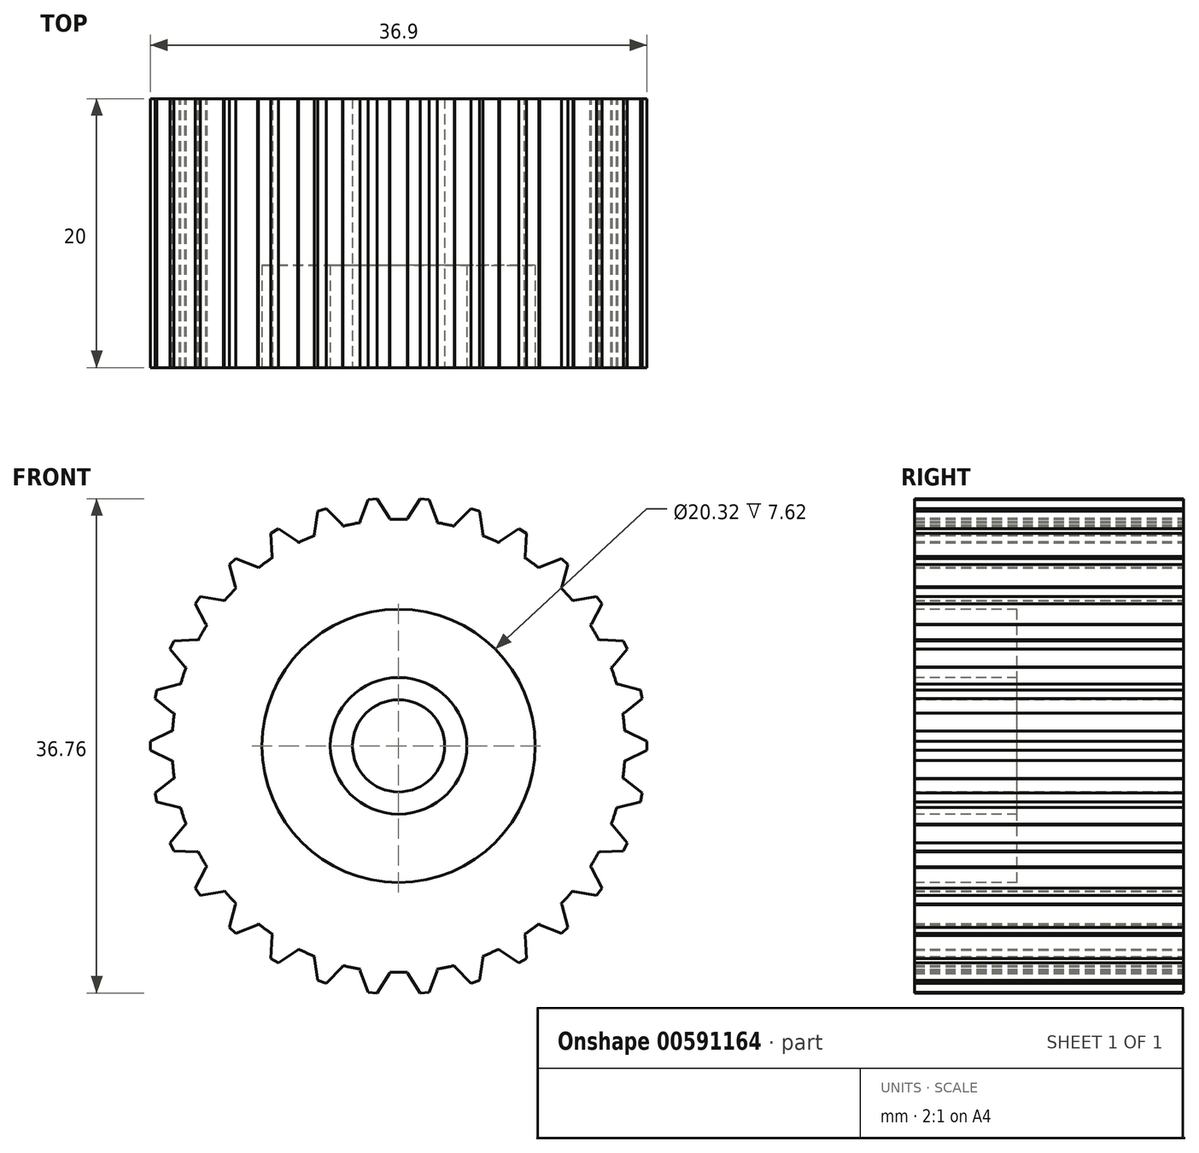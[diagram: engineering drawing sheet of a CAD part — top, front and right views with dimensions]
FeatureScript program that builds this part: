
annotation { "Feature Type Name" : "Feature", "Feature Type Description" : "" }
export const myFeature = defineFeature(function(context is Context, id is Id, definition is map)
    precondition{}
    {
        {
            var Q0;
            Q0=qCreatedBy(makeId("Front.planeOp"),FACE);
            var sketch = newSketch(context, id + "F0", { "sketchPlane" : qUnion([Q0])});
            skCircle(sketch, "E0", {"center": v(0, 0) * mm, "radius": 16.85 * mm});
            skLineSegment(sketch, "E1", {"start": v(0, 0) * mm, "end": v(16.85, 0) * mm, "construction": true});
            skLineSegment(sketch, "E2", {"start": v(16.85, 0) * mm, "end": v(18.45, 0) * mm, "construction": true});
            skLineSegment(sketch, "E3", {"start": v(18.45, 0) * mm, "end": v(18.45, 0.33) * mm});
            skLineSegment(sketch, "E4", {"start": v(16.81, 1.1) * mm, "end": v(16.91, 1.1) * mm});
            skLineSegment(sketch, "E5", {"start": v(16.91, 1.1) * mm, "end": v(18.45, 0.33) * mm});
            skLineSegment(sketch, "E6.MirrorCS", {"start": v(16.91, -1.1) * mm, "end": v(18.45, -0.33) * mm});
            skLineSegment(sketch, "E7.MirrorCS", {"start": v(18.45, 0) * mm, "end": v(18.45, -0.33) * mm});
            skLineSegment(sketch, "E8.MirrorCS", {"start": v(16.81, -1.1) * mm, "end": v(16.91, -1.1) * mm});
            skLineSegment(sketch, "E9.2.0", {"start": v(-72.23, -20.11) * mm, "end": v(-72.15, -20.06) * mm});
            skLineSegment(sketch, "E9.2.1", {"start": v(-72.15, -20.06) * mm, "end": v(-71.63, -19.91) * mm});
            skLineSegment(sketch, "E9.2.2", {"start": v(-71.45, -20.19) * mm, "end": v(-71.63, -19.91) * mm});
            skLineSegment(sketch, "E9.2.3", {"start": v(-71.45, -20.19) * mm, "end": v(-71.26, -20.46) * mm});
            skLineSegment(sketch, "E9.2.4", {"start": v(-71.58, -20.88) * mm, "end": v(-71.26, -20.46) * mm});
            skLineSegment(sketch, "E9.2.5", {"start": v(-71.67, -20.94) * mm, "end": v(-71.58, -20.88) * mm});
            skLineSegment(sketch, "E9.3.0", {"start": v(-108.67, -49.23) * mm, "end": v(-108.6, -49.15) * mm});
            skLineSegment(sketch, "E9.3.1", {"start": v(-108.6, -49.15) * mm, "end": v(-108.16, -48.86) * mm});
            skLineSegment(sketch, "E9.3.2", {"start": v(-107.9, -49.07) * mm, "end": v(-108.16, -48.86) * mm});
            skLineSegment(sketch, "E9.3.3", {"start": v(-107.9, -49.07) * mm, "end": v(-107.64, -49.28) * mm});
            skLineSegment(sketch, "E9.3.4", {"start": v(-107.83, -49.78) * mm, "end": v(-107.64, -49.28) * mm});
            skLineSegment(sketch, "E9.3.5", {"start": v(-107.89, -49.86) * mm, "end": v(-107.83, -49.78) * mm});
            skLineSegment(sketch, "E9.4.0", {"start": v(-134.91, -87.8) * mm, "end": v(-134.88, -87.7) * mm});
            skLineSegment(sketch, "E9.4.1", {"start": v(-134.88, -87.7) * mm, "end": v(-134.53, -87.3) * mm});
            skLineSegment(sketch, "E9.4.2", {"start": v(-134.23, -87.42) * mm, "end": v(-134.53, -87.3) * mm});
            skLineSegment(sketch, "E9.4.3", {"start": v(-134.23, -87.42) * mm, "end": v(-133.92, -87.54) * mm});
            skLineSegment(sketch, "E9.4.4", {"start": v(-133.95, -88.07) * mm, "end": v(-133.92, -87.54) * mm});
            skLineSegment(sketch, "E9.4.5", {"start": v(-133.98, -88.17) * mm, "end": v(-133.95, -88.07) * mm});
            skLineSegment(sketch, "E9.5.0", {"start": v(-148.62, -132.39) * mm, "end": v(-148.61, -132.29) * mm});
            skLineSegment(sketch, "E9.5.1", {"start": v(-148.61, -132.29) * mm, "end": v(-148.4, -131.8) * mm});
            skLineSegment(sketch, "E9.5.2", {"start": v(-148.08, -131.82) * mm, "end": v(-148.4, -131.8) * mm});
            skLineSegment(sketch, "E9.5.3", {"start": v(-148.08, -131.82) * mm, "end": v(-147.75, -131.85) * mm});
            skLineSegment(sketch, "E9.5.4", {"start": v(-147.62, -132.36) * mm, "end": v(-147.75, -131.85) * mm});
            skLineSegment(sketch, "E9.5.5", {"start": v(-147.62, -132.46) * mm, "end": v(-147.62, -132.36) * mm});
            skLineSegment(sketch, "E9.6.0", {"start": v(-148.58, -179.04) * mm, "end": v(-148.6, -178.94) * mm});
            skLineSegment(sketch, "E9.6.1", {"start": v(-148.6, -178.94) * mm, "end": v(-148.54, -178.4) * mm});
            skLineSegment(sketch, "E9.6.2", {"start": v(-148.22, -178.33) * mm, "end": v(-148.54, -178.4) * mm});
            skLineSegment(sketch, "E9.6.3", {"start": v(-148.22, -178.33) * mm, "end": v(-147.9, -178.26) * mm});
            skLineSegment(sketch, "E9.6.4", {"start": v(-147.62, -178.72) * mm, "end": v(-147.9, -178.26) * mm});
            skLineSegment(sketch, "E9.6.5", {"start": v(-147.6, -178.81) * mm, "end": v(-147.62, -178.72) * mm});
            skLineSegment(sketch, "E9.7.0", {"start": v(-134.78, -223.6) * mm, "end": v(-134.83, -223.51) * mm});
            skLineSegment(sketch, "E9.7.1", {"start": v(-134.83, -223.51) * mm, "end": v(-134.94, -222.99) * mm});
            skLineSegment(sketch, "E9.7.2", {"start": v(-134.65, -222.82) * mm, "end": v(-134.94, -222.99) * mm});
            skLineSegment(sketch, "E9.7.3", {"start": v(-134.65, -222.82) * mm, "end": v(-134.37, -222.66) * mm});
            skLineSegment(sketch, "E9.7.4", {"start": v(-133.97, -223.01) * mm, "end": v(-134.37, -222.66) * mm});
            skLineSegment(sketch, "E9.7.5", {"start": v(-133.92, -223.1) * mm, "end": v(-133.97, -223.01) * mm});
            skLineSegment(sketch, "E9.8.0", {"start": v(-108.47, -262.12) * mm, "end": v(-108.54, -262.05) * mm});
            skLineSegment(sketch, "E9.8.1", {"start": v(-108.54, -262.05) * mm, "end": v(-108.8, -261.58) * mm});
            skLineSegment(sketch, "E9.8.2", {"start": v(-108.57, -261.34) * mm, "end": v(-108.8, -261.58) * mm});
            skLineSegment(sketch, "E9.8.3", {"start": v(-108.57, -261.34) * mm, "end": v(-108.35, -261.1) * mm});
            skLineSegment(sketch, "E9.8.4", {"start": v(-107.86, -261.32) * mm, "end": v(-108.35, -261.1) * mm});
            skLineSegment(sketch, "E9.8.5", {"start": v(-107.79, -261.38) * mm, "end": v(-107.86, -261.32) * mm});
            skLineSegment(sketch, "E9.9.0", {"start": v(-71.97, -291.17) * mm, "end": v(-72.06, -291.12) * mm});
            skLineSegment(sketch, "E9.9.1", {"start": v(-72.06, -291.12) * mm, "end": v(-72.44, -290.75) * mm});
            skLineSegment(sketch, "E9.9.2", {"start": v(-72.3, -290.45) * mm, "end": v(-72.44, -290.75) * mm});
            skLineSegment(sketch, "E9.9.3", {"start": v(-72.3, -290.45) * mm, "end": v(-72.16, -290.16) * mm});
            skLineSegment(sketch, "E9.9.4", {"start": v(-71.63, -290.22) * mm, "end": v(-72.16, -290.16) * mm});
            skLineSegment(sketch, "E9.9.5", {"start": v(-71.54, -290.27) * mm, "end": v(-71.63, -290.22) * mm});
            skLineSegment(sketch, "E9.10.0", {"start": v(-28.53, -308.17) * mm, "end": v(-28.63, -308.15) * mm});
            skLineSegment(sketch, "E9.10.1", {"start": v(-28.63, -308.15) * mm, "end": v(-29.1, -307.9) * mm});
            skLineSegment(sketch, "E9.10.2", {"start": v(-29.06, -307.58) * mm, "end": v(-29.1, -307.9) * mm});
            skLineSegment(sketch, "E9.10.3", {"start": v(-29.06, -307.58) * mm, "end": v(-29, -307.26) * mm});
            skLineSegment(sketch, "E9.10.4", {"start": v(-28.48, -307.16) * mm, "end": v(-29, -307.26) * mm});
            skLineSegment(sketch, "E9.10.5", {"start": v(-28.38, -307.18) * mm, "end": v(-28.48, -307.16) * mm});
            skLineSegment(sketch, "E9.11.0", {"start": v(17.99, -311.6) * mm, "end": v(17.9, -311.62) * mm});
            skLineSegment(sketch, "E9.11.1", {"start": v(17.9, -311.62) * mm, "end": v(17.36, -311.53) * mm});
            skLineSegment(sketch, "E9.11.2", {"start": v(17.31, -311.2) * mm, "end": v(17.36, -311.53) * mm});
            skLineSegment(sketch, "E9.11.3", {"start": v(17.31, -311.2) * mm, "end": v(17.27, -310.88) * mm});
            skLineSegment(sketch, "E9.11.4", {"start": v(17.74, -310.64) * mm, "end": v(17.27, -310.88) * mm});
            skLineSegment(sketch, "E9.11.5", {"start": v(17.84, -310.62) * mm, "end": v(17.74, -310.64) * mm});
            skLineSegment(sketch, "E9.12.0", {"start": v(63.46, -301.19) * mm, "end": v(63.37, -301.23) * mm});
            skLineSegment(sketch, "E9.12.1", {"start": v(63.37, -301.23) * mm, "end": v(62.84, -301.3) * mm});
            skLineSegment(sketch, "E9.12.2", {"start": v(62.7, -301) * mm, "end": v(62.84, -301.3) * mm});
            skLineSegment(sketch, "E9.12.3", {"start": v(62.7, -301) * mm, "end": v(62.55, -300.7) * mm});
            skLineSegment(sketch, "E9.12.4", {"start": v(62.93, -300.33) * mm, "end": v(62.55, -300.7) * mm});
            skLineSegment(sketch, "E9.12.5", {"start": v(63.02, -300.28) * mm, "end": v(62.93, -300.33) * mm});
            skLineSegment(sketch, "E9.13.0", {"start": v(103.83, -277.82) * mm, "end": v(103.76, -277.9) * mm});
            skLineSegment(sketch, "E9.13.1", {"start": v(103.76, -277.9) * mm, "end": v(103.27, -278.11) * mm});
            skLineSegment(sketch, "E9.13.2", {"start": v(103.05, -277.87) * mm, "end": v(103.27, -278.11) * mm});
            skLineSegment(sketch, "E9.13.3", {"start": v(103.05, -277.87) * mm, "end": v(102.82, -277.63) * mm});
            skLineSegment(sketch, "E9.13.4", {"start": v(103.08, -277.16) * mm, "end": v(102.82, -277.63) * mm});
            skLineSegment(sketch, "E9.13.5", {"start": v(103.15, -277.1) * mm, "end": v(103.08, -277.16) * mm});
            skLineSegment(sketch, "E9.14.0", {"start": v(135.53, -243.6) * mm, "end": v(135.48, -243.68) * mm});
            skLineSegment(sketch, "E9.14.1", {"start": v(135.48, -243.68) * mm, "end": v(135.08, -244.04) * mm});
            skLineSegment(sketch, "E9.14.2", {"start": v(134.8, -243.87) * mm, "end": v(135.08, -244.04) * mm});
            skLineSegment(sketch, "E9.14.3", {"start": v(134.8, -243.87) * mm, "end": v(134.5, -243.7) * mm});
            skLineSegment(sketch, "E9.14.4", {"start": v(134.61, -243.18) * mm, "end": v(134.5, -243.7) * mm});
            skLineSegment(sketch, "E9.14.5", {"start": v(134.66, -243.1) * mm, "end": v(134.61, -243.18) * mm});
            skLineSegment(sketch, "E9.15.0", {"start": v(155.73, -201.55) * mm, "end": v(155.7, -201.65) * mm});
            skLineSegment(sketch, "E9.15.1", {"start": v(155.7, -201.65) * mm, "end": v(155.43, -202.1) * mm});
            skLineSegment(sketch, "E9.15.2", {"start": v(155.1, -202.03) * mm, "end": v(155.43, -202.1) * mm});
            skLineSegment(sketch, "E9.15.3", {"start": v(155.1, -202.03) * mm, "end": v(154.79, -201.96) * mm});
            skLineSegment(sketch, "E9.15.4", {"start": v(154.73, -201.43) * mm, "end": v(154.79, -201.96) * mm});
            skLineSegment(sketch, "E9.15.5", {"start": v(154.76, -201.33) * mm, "end": v(154.73, -201.43) * mm});
            skLineSegment(sketch, "E9.16.0", {"start": v(162.64, -155.42) * mm, "end": v(162.65, -155.52) * mm});
            skLineSegment(sketch, "E9.16.1", {"start": v(162.65, -155.52) * mm, "end": v(162.51, -156.04) * mm});
            skLineSegment(sketch, "E9.16.2", {"start": v(162.19, -156.06) * mm, "end": v(162.51, -156.04) * mm});
            skLineSegment(sketch, "E9.16.3", {"start": v(162.19, -156.06) * mm, "end": v(161.86, -156.08) * mm});
            skLineSegment(sketch, "E9.16.4", {"start": v(161.65, -155.6) * mm, "end": v(161.86, -156.08) * mm});
            skLineSegment(sketch, "E9.16.5", {"start": v(161.64, -155.5) * mm, "end": v(161.65, -155.6) * mm});
            skLineSegment(sketch, "E9.17.0", {"start": v(155.64, -109.3) * mm, "end": v(155.68, -109.39) * mm});
            skLineSegment(sketch, "E9.17.1", {"start": v(155.68, -109.39) * mm, "end": v(155.7, -109.92) * mm});
            skLineSegment(sketch, "E9.17.2", {"start": v(155.4, -110.04) * mm, "end": v(155.7, -109.92) * mm});
            skLineSegment(sketch, "E9.17.3", {"start": v(155.4, -110.04) * mm, "end": v(155.1, -110.17) * mm});
            skLineSegment(sketch, "E9.17.4", {"start": v(154.75, -109.76) * mm, "end": v(155.1, -110.17) * mm});
            skLineSegment(sketch, "E9.17.5", {"start": v(154.71, -109.66) * mm, "end": v(154.75, -109.76) * mm});
            skLineSegment(sketch, "E9.18.0", {"start": v(135.36, -67.29) * mm, "end": v(135.43, -67.37) * mm});
            skLineSegment(sketch, "E9.18.1", {"start": v(135.43, -67.37) * mm, "end": v(135.6, -67.87) * mm});
            skLineSegment(sketch, "E9.18.2", {"start": v(135.35, -68.07) * mm, "end": v(135.6, -67.87) * mm});
            skLineSegment(sketch, "E9.18.3", {"start": v(135.35, -68.07) * mm, "end": v(135.1, -68.28) * mm});
            skLineSegment(sketch, "E9.18.4", {"start": v(134.64, -67.99) * mm, "end": v(135.1, -68.28) * mm});
            skLineSegment(sketch, "E9.18.5", {"start": v(134.58, -67.91) * mm, "end": v(134.64, -67.99) * mm});
            skLineSegment(sketch, "E9.19.0", {"start": v(103.6, -33.12) * mm, "end": v(103.68, -33.18) * mm});
            skLineSegment(sketch, "E9.19.1", {"start": v(103.68, -33.18) * mm, "end": v(104, -33.6) * mm});
            skLineSegment(sketch, "E9.19.2", {"start": v(103.82, -33.88) * mm, "end": v(104, -33.6) * mm});
            skLineSegment(sketch, "E9.19.3", {"start": v(103.82, -33.88) * mm, "end": v(103.64, -34.15) * mm});
            skLineSegment(sketch, "E9.19.4", {"start": v(103.12, -34) * mm, "end": v(103.64, -34.15) * mm});
            skLineSegment(sketch, "E9.19.5", {"start": v(103.04, -33.95) * mm, "end": v(103.12, -34) * mm});
            skLineSegment(sketch, "E9.20.0", {"start": v(63.18, -9.84) * mm, "end": v(63.28, -9.87) * mm});
            skLineSegment(sketch, "E9.20.1", {"start": v(63.28, -9.87) * mm, "end": v(63.71, -10.18) * mm});
            skLineSegment(sketch, "E9.20.2", {"start": v(63.61, -10.5) * mm, "end": v(63.71, -10.18) * mm});
            skLineSegment(sketch, "E9.20.3", {"start": v(63.61, -10.5) * mm, "end": v(63.52, -10.8) * mm});
            skLineSegment(sketch, "E9.20.4", {"start": v(62.98, -10.82) * mm, "end": v(63.52, -10.8) * mm});
            skLineSegment(sketch, "E9.20.5", {"start": v(62.89, -10.8) * mm, "end": v(62.98, -10.82) * mm});
            skPoint(sketch, "E10.center", {"position": v(-0.17, 0) * mm});
            skLineSegment(sketch, "E11.1.0", {"start": v(16.22, 4.57) * mm, "end": v(16.32, 4.6) * mm});
            skLineSegment(sketch, "E11.1.1", {"start": v(16.32, 4.6) * mm, "end": v(17.98, 4.16) * mm});
            skLineSegment(sketch, "E11.1.2", {"start": v(18.05, 3.84) * mm, "end": v(17.98, 4.16) * mm});
            skLineSegment(sketch, "E11.1.3", {"start": v(18.05, 3.84) * mm, "end": v(18.12, 3.51) * mm});
            skLineSegment(sketch, "E11.1.4", {"start": v(16.77, 2.44) * mm, "end": v(18.12, 3.51) * mm});
            skLineSegment(sketch, "E11.1.5", {"start": v(16.68, 2.42) * mm, "end": v(16.77, 2.44) * mm});
            skLineSegment(sketch, "E11.2.0", {"start": v(14.91, 7.84) * mm, "end": v(15, 7.88) * mm});
            skLineSegment(sketch, "E11.2.1", {"start": v(15, 7.88) * mm, "end": v(16.72, 7.8) * mm});
            skLineSegment(sketch, "E11.2.2", {"start": v(16.85, 7.5) * mm, "end": v(16.72, 7.8) * mm});
            skLineSegment(sketch, "E11.2.3", {"start": v(16.85, 7.5) * mm, "end": v(16.99, 7.2) * mm});
            skLineSegment(sketch, "E11.2.4", {"start": v(15.9, 5.87) * mm, "end": v(16.99, 7.2) * mm});
            skLineSegment(sketch, "E11.2.5", {"start": v(15.8, 5.83) * mm, "end": v(15.9, 5.87) * mm});
            skLineSegment(sketch, "E11.3.0", {"start": v(12.96, 10.77) * mm, "end": v(13.04, 10.83) * mm});
            skLineSegment(sketch, "E11.3.1", {"start": v(13.04, 10.83) * mm, "end": v(14.73, 11.11) * mm});
            skLineSegment(sketch, "E11.3.2", {"start": v(14.93, 10.84) * mm, "end": v(14.73, 11.11) * mm});
            skLineSegment(sketch, "E11.3.3", {"start": v(14.93, 10.84) * mm, "end": v(15.12, 10.58) * mm});
            skLineSegment(sketch, "E11.3.4", {"start": v(14.33, 9.05) * mm, "end": v(15.12, 10.58) * mm});
            skLineSegment(sketch, "E11.3.5", {"start": v(14.25, 9) * mm, "end": v(14.33, 9.05) * mm});
            skLineSegment(sketch, "E11.4.0", {"start": v(10.43, 13.23) * mm, "end": v(10.5, 13.3) * mm});
            skLineSegment(sketch, "E11.4.1", {"start": v(10.5, 13.3) * mm, "end": v(12.1, 13.93) * mm});
            skLineSegment(sketch, "E11.4.2", {"start": v(12.35, 13.71) * mm, "end": v(12.1, 13.93) * mm});
            skLineSegment(sketch, "E11.4.3", {"start": v(12.35, 13.71) * mm, "end": v(12.6, 13.5) * mm});
            skLineSegment(sketch, "E11.4.4", {"start": v(12.14, 11.83) * mm, "end": v(12.6, 13.5) * mm});
            skLineSegment(sketch, "E11.4.5", {"start": v(12.07, 11.76) * mm, "end": v(12.14, 11.83) * mm});
            skLineSegment(sketch, "E11.5.0", {"start": v(7.45, 15.11) * mm, "end": v(7.5, 15.2) * mm});
            skLineSegment(sketch, "E11.5.1", {"start": v(7.5, 15.2) * mm, "end": v(8.94, 16.14) * mm});
            skLineSegment(sketch, "E11.5.2", {"start": v(9.22, 15.98) * mm, "end": v(8.94, 16.14) * mm});
            skLineSegment(sketch, "E11.5.3", {"start": v(9.23, 15.98) * mm, "end": v(9.51, 15.81) * mm});
            skLineSegment(sketch, "E11.5.4", {"start": v(9.4, 14.1) * mm, "end": v(9.51, 15.81) * mm});
            skLineSegment(sketch, "E11.5.5", {"start": v(9.36, 14.01) * mm, "end": v(9.4, 14.1) * mm});
            skLineSegment(sketch, "E11.6.0", {"start": v(4.15, 16.33) * mm, "end": v(4.18, 16.43) * mm});
            skLineSegment(sketch, "E11.6.1", {"start": v(4.18, 16.43) * mm, "end": v(5.39, 17.65) * mm});
            skLineSegment(sketch, "E11.6.2", {"start": v(5.7, 17.55) * mm, "end": v(5.39, 17.65) * mm});
            skLineSegment(sketch, "E11.6.3", {"start": v(5.7, 17.55) * mm, "end": v(6.02, 17.45) * mm});
            skLineSegment(sketch, "E11.6.4", {"start": v(6.27, 15.75) * mm, "end": v(6.02, 17.45) * mm});
            skLineSegment(sketch, "E11.6.5", {"start": v(6.24, 15.65) * mm, "end": v(6.27, 15.75) * mm});
            skLineSegment(sketch, "E11.7.0", {"start": v(0.66, 16.84) * mm, "end": v(0.67, 16.94) * mm});
            skLineSegment(sketch, "E11.7.1", {"start": v(0.67, 16.94) * mm, "end": v(1.6, 18.38) * mm});
            skLineSegment(sketch, "E11.7.2", {"start": v(1.93, 18.35) * mm, "end": v(1.6, 18.38) * mm});
            skLineSegment(sketch, "E11.7.3", {"start": v(1.93, 18.35) * mm, "end": v(2.26, 18.31) * mm});
            skLineSegment(sketch, "E11.7.4", {"start": v(2.86, 16.7) * mm, "end": v(2.26, 18.31) * mm});
            skLineSegment(sketch, "E11.7.5", {"start": v(2.85, 16.6) * mm, "end": v(2.86, 16.7) * mm});
            skLineSegment(sketch, "E11.8.0", {"start": v(-2.85, 16.6) * mm, "end": v(-2.86, 16.7) * mm});
            skLineSegment(sketch, "E11.8.1", {"start": v(-2.86, 16.7) * mm, "end": v(-2.26, 18.31) * mm});
            skLineSegment(sketch, "E11.8.2", {"start": v(-1.93, 18.35) * mm, "end": v(-2.26, 18.31) * mm});
            skLineSegment(sketch, "E11.8.3", {"start": v(-1.93, 18.35) * mm, "end": v(-1.6, 18.38) * mm});
            skLineSegment(sketch, "E11.8.4", {"start": v(-0.67, 16.94) * mm, "end": v(-1.6, 18.38) * mm});
            skLineSegment(sketch, "E11.8.5", {"start": v(-0.66, 16.84) * mm, "end": v(-0.67, 16.94) * mm});
            skLineSegment(sketch, "E11.9.0", {"start": v(-6.24, 15.65) * mm, "end": v(-6.27, 15.75) * mm});
            skLineSegment(sketch, "E11.9.1", {"start": v(-6.27, 15.75) * mm, "end": v(-6.02, 17.45) * mm});
            skLineSegment(sketch, "E11.9.2", {"start": v(-5.7, 17.55) * mm, "end": v(-6.02, 17.45) * mm});
            skLineSegment(sketch, "E11.9.3", {"start": v(-5.7, 17.55) * mm, "end": v(-5.39, 17.65) * mm});
            skLineSegment(sketch, "E11.9.4", {"start": v(-4.18, 16.43) * mm, "end": v(-5.39, 17.65) * mm});
            skLineSegment(sketch, "E11.9.5", {"start": v(-4.15, 16.33) * mm, "end": v(-4.18, 16.43) * mm});
            skLineSegment(sketch, "E11.10.0", {"start": v(-9.36, 14.01) * mm, "end": v(-9.4, 14.1) * mm});
            skLineSegment(sketch, "E11.10.1", {"start": v(-9.4, 14.1) * mm, "end": v(-9.51, 15.81) * mm});
            skLineSegment(sketch, "E11.10.2", {"start": v(-9.23, 15.98) * mm, "end": v(-9.51, 15.81) * mm});
            skLineSegment(sketch, "E11.10.3", {"start": v(-9.23, 15.98) * mm, "end": v(-8.94, 16.14) * mm});
            skLineSegment(sketch, "E11.10.4", {"start": v(-7.5, 15.2) * mm, "end": v(-8.94, 16.14) * mm});
            skLineSegment(sketch, "E11.10.5", {"start": v(-7.45, 15.11) * mm, "end": v(-7.5, 15.2) * mm});
            skLineSegment(sketch, "E11.11.0", {"start": v(-12.07, 11.76) * mm, "end": v(-12.14, 11.83) * mm});
            skLineSegment(sketch, "E11.11.1", {"start": v(-12.14, 11.83) * mm, "end": v(-12.6, 13.5) * mm});
            skLineSegment(sketch, "E11.11.2", {"start": v(-12.35, 13.71) * mm, "end": v(-12.6, 13.5) * mm});
            skLineSegment(sketch, "E11.11.3", {"start": v(-12.35, 13.71) * mm, "end": v(-12.1, 13.93) * mm});
            skLineSegment(sketch, "E11.11.4", {"start": v(-10.5, 13.3) * mm, "end": v(-12.1, 13.93) * mm});
            skLineSegment(sketch, "E11.11.5", {"start": v(-10.43, 13.23) * mm, "end": v(-10.5, 13.3) * mm});
            skLineSegment(sketch, "E11.12.0", {"start": v(-14.25, 9) * mm, "end": v(-14.33, 9.05) * mm});
            skLineSegment(sketch, "E11.12.1", {"start": v(-14.33, 9.05) * mm, "end": v(-15.12, 10.58) * mm});
            skLineSegment(sketch, "E11.12.2", {"start": v(-14.93, 10.84) * mm, "end": v(-15.12, 10.58) * mm});
            skLineSegment(sketch, "E11.12.3", {"start": v(-14.93, 10.84) * mm, "end": v(-14.73, 11.11) * mm});
            skLineSegment(sketch, "E11.12.4", {"start": v(-13.04, 10.83) * mm, "end": v(-14.73, 11.11) * mm});
            skLineSegment(sketch, "E11.12.5", {"start": v(-12.96, 10.77) * mm, "end": v(-13.04, 10.83) * mm});
            skLineSegment(sketch, "E11.13.0", {"start": v(-15.8, 5.83) * mm, "end": v(-15.9, 5.87) * mm});
            skLineSegment(sketch, "E11.13.1", {"start": v(-15.9, 5.87) * mm, "end": v(-16.99, 7.2) * mm});
            skLineSegment(sketch, "E11.13.2", {"start": v(-16.85, 7.5) * mm, "end": v(-16.99, 7.2) * mm});
            skLineSegment(sketch, "E11.13.3", {"start": v(-16.85, 7.5) * mm, "end": v(-16.72, 7.8) * mm});
            skLineSegment(sketch, "E11.13.4", {"start": v(-15, 7.88) * mm, "end": v(-16.72, 7.8) * mm});
            skLineSegment(sketch, "E11.13.5", {"start": v(-14.91, 7.84) * mm, "end": v(-15, 7.88) * mm});
            skLineSegment(sketch, "E11.14.0", {"start": v(-16.68, 2.42) * mm, "end": v(-16.77, 2.44) * mm});
            skLineSegment(sketch, "E11.14.1", {"start": v(-16.77, 2.44) * mm, "end": v(-18.12, 3.51) * mm});
            skLineSegment(sketch, "E11.14.2", {"start": v(-18.05, 3.84) * mm, "end": v(-18.12, 3.51) * mm});
            skLineSegment(sketch, "E11.14.3", {"start": v(-18.05, 3.84) * mm, "end": v(-17.98, 4.16) * mm});
            skLineSegment(sketch, "E11.14.4", {"start": v(-16.32, 4.6) * mm, "end": v(-17.98, 4.16) * mm});
            skLineSegment(sketch, "E11.14.5", {"start": v(-16.22, 4.57) * mm, "end": v(-16.32, 4.6) * mm});
            skLineSegment(sketch, "E11.15.0", {"start": v(-16.81, -1.1) * mm, "end": v(-16.91, -1.1) * mm});
            skLineSegment(sketch, "E11.15.1", {"start": v(-16.91, -1.1) * mm, "end": v(-18.45, -0.33) * mm});
            skLineSegment(sketch, "E11.15.2", {"start": v(-18.45, 0) * mm, "end": v(-18.45, -0.33) * mm});
            skLineSegment(sketch, "E11.15.3", {"start": v(-18.45, 0) * mm, "end": v(-18.45, 0.33) * mm});
            skLineSegment(sketch, "E11.15.4", {"start": v(-16.91, 1.1) * mm, "end": v(-18.45, 0.33) * mm});
            skLineSegment(sketch, "E11.15.5", {"start": v(-16.81, 1.1) * mm, "end": v(-16.91, 1.1) * mm});
            skLineSegment(sketch, "E11.16.0", {"start": v(-16.22, -4.57) * mm, "end": v(-16.32, -4.6) * mm});
            skLineSegment(sketch, "E11.16.1", {"start": v(-16.32, -4.6) * mm, "end": v(-17.98, -4.16) * mm});
            skLineSegment(sketch, "E11.16.2", {"start": v(-18.05, -3.84) * mm, "end": v(-17.98, -4.16) * mm});
            skLineSegment(sketch, "E11.16.3", {"start": v(-18.05, -3.84) * mm, "end": v(-18.12, -3.51) * mm});
            skLineSegment(sketch, "E11.16.4", {"start": v(-16.77, -2.44) * mm, "end": v(-18.12, -3.51) * mm});
            skLineSegment(sketch, "E11.16.5", {"start": v(-16.68, -2.42) * mm, "end": v(-16.77, -2.44) * mm});
            skLineSegment(sketch, "E11.17.0", {"start": v(-14.91, -7.84) * mm, "end": v(-15, -7.88) * mm});
            skLineSegment(sketch, "E11.17.1", {"start": v(-15, -7.88) * mm, "end": v(-16.72, -7.8) * mm});
            skLineSegment(sketch, "E11.17.2", {"start": v(-16.85, -7.5) * mm, "end": v(-16.72, -7.8) * mm});
            skLineSegment(sketch, "E11.17.3", {"start": v(-16.85, -7.5) * mm, "end": v(-16.99, -7.2) * mm});
            skLineSegment(sketch, "E11.17.4", {"start": v(-15.9, -5.87) * mm, "end": v(-16.99, -7.2) * mm});
            skLineSegment(sketch, "E11.17.5", {"start": v(-15.8, -5.83) * mm, "end": v(-15.9, -5.87) * mm});
            skLineSegment(sketch, "E11.18.0", {"start": v(-12.96, -10.77) * mm, "end": v(-13.04, -10.83) * mm});
            skLineSegment(sketch, "E11.18.1", {"start": v(-13.04, -10.83) * mm, "end": v(-14.73, -11.11) * mm});
            skLineSegment(sketch, "E11.18.2", {"start": v(-14.93, -10.84) * mm, "end": v(-14.73, -11.11) * mm});
            skLineSegment(sketch, "E11.18.3", {"start": v(-14.93, -10.84) * mm, "end": v(-15.12, -10.58) * mm});
            skLineSegment(sketch, "E11.18.4", {"start": v(-14.33, -9.05) * mm, "end": v(-15.12, -10.58) * mm});
            skLineSegment(sketch, "E11.18.5", {"start": v(-14.25, -9) * mm, "end": v(-14.33, -9.05) * mm});
            skLineSegment(sketch, "E11.19.0", {"start": v(-10.43, -13.23) * mm, "end": v(-10.5, -13.3) * mm});
            skLineSegment(sketch, "E11.19.1", {"start": v(-10.5, -13.3) * mm, "end": v(-12.1, -13.93) * mm});
            skLineSegment(sketch, "E11.19.2", {"start": v(-12.35, -13.71) * mm, "end": v(-12.1, -13.93) * mm});
            skLineSegment(sketch, "E11.19.3", {"start": v(-12.35, -13.71) * mm, "end": v(-12.6, -13.5) * mm});
            skLineSegment(sketch, "E11.19.4", {"start": v(-12.14, -11.83) * mm, "end": v(-12.6, -13.5) * mm});
            skLineSegment(sketch, "E11.19.5", {"start": v(-12.07, -11.76) * mm, "end": v(-12.14, -11.83) * mm});
            skLineSegment(sketch, "E11.20.0", {"start": v(-7.45, -15.11) * mm, "end": v(-7.5, -15.2) * mm});
            skLineSegment(sketch, "E11.20.1", {"start": v(-7.5, -15.2) * mm, "end": v(-8.94, -16.14) * mm});
            skLineSegment(sketch, "E11.20.2", {"start": v(-9.23, -15.98) * mm, "end": v(-8.94, -16.14) * mm});
            skLineSegment(sketch, "E11.20.3", {"start": v(-9.23, -15.98) * mm, "end": v(-9.51, -15.81) * mm});
            skLineSegment(sketch, "E11.20.4", {"start": v(-9.4, -14.1) * mm, "end": v(-9.51, -15.81) * mm});
            skLineSegment(sketch, "E11.20.5", {"start": v(-9.36, -14.01) * mm, "end": v(-9.4, -14.1) * mm});
            skLineSegment(sketch, "E11.21.0", {"start": v(-4.15, -16.33) * mm, "end": v(-4.18, -16.43) * mm});
            skLineSegment(sketch, "E11.21.1", {"start": v(-4.18, -16.43) * mm, "end": v(-5.39, -17.65) * mm});
            skLineSegment(sketch, "E11.21.2", {"start": v(-5.7, -17.55) * mm, "end": v(-5.39, -17.65) * mm});
            skLineSegment(sketch, "E11.21.3", {"start": v(-5.7, -17.55) * mm, "end": v(-6.02, -17.45) * mm});
            skLineSegment(sketch, "E11.21.4", {"start": v(-6.27, -15.75) * mm, "end": v(-6.02, -17.45) * mm});
            skLineSegment(sketch, "E11.21.5", {"start": v(-6.24, -15.65) * mm, "end": v(-6.27, -15.75) * mm});
            skLineSegment(sketch, "E11.22.0", {"start": v(-0.66, -16.84) * mm, "end": v(-0.67, -16.94) * mm});
            skLineSegment(sketch, "E11.22.1", {"start": v(-0.67, -16.94) * mm, "end": v(-1.6, -18.38) * mm});
            skLineSegment(sketch, "E11.22.2", {"start": v(-1.93, -18.35) * mm, "end": v(-1.6, -18.38) * mm});
            skLineSegment(sketch, "E11.22.3", {"start": v(-1.93, -18.35) * mm, "end": v(-2.26, -18.31) * mm});
            skLineSegment(sketch, "E11.22.4", {"start": v(-2.86, -16.7) * mm, "end": v(-2.26, -18.31) * mm});
            skLineSegment(sketch, "E11.22.5", {"start": v(-2.85, -16.6) * mm, "end": v(-2.86, -16.7) * mm});
            skLineSegment(sketch, "E11.23.0", {"start": v(2.85, -16.6) * mm, "end": v(2.86, -16.7) * mm});
            skLineSegment(sketch, "E11.23.1", {"start": v(2.86, -16.7) * mm, "end": v(2.26, -18.31) * mm});
            skLineSegment(sketch, "E11.23.2", {"start": v(1.93, -18.35) * mm, "end": v(2.26, -18.31) * mm});
            skLineSegment(sketch, "E11.23.3", {"start": v(1.93, -18.35) * mm, "end": v(1.6, -18.38) * mm});
            skLineSegment(sketch, "E11.23.4", {"start": v(0.67, -16.94) * mm, "end": v(1.6, -18.38) * mm});
            skLineSegment(sketch, "E11.23.5", {"start": v(0.66, -16.84) * mm, "end": v(0.67, -16.94) * mm});
            skLineSegment(sketch, "E11.24.0", {"start": v(6.24, -15.65) * mm, "end": v(6.27, -15.75) * mm});
            skLineSegment(sketch, "E11.24.1", {"start": v(6.27, -15.75) * mm, "end": v(6.02, -17.45) * mm});
            skLineSegment(sketch, "E11.24.2", {"start": v(5.7, -17.55) * mm, "end": v(6.02, -17.45) * mm});
            skLineSegment(sketch, "E11.24.3", {"start": v(5.7, -17.55) * mm, "end": v(5.39, -17.65) * mm});
            skLineSegment(sketch, "E11.24.4", {"start": v(4.18, -16.43) * mm, "end": v(5.39, -17.65) * mm});
            skLineSegment(sketch, "E11.24.5", {"start": v(4.15, -16.33) * mm, "end": v(4.18, -16.43) * mm});
            skLineSegment(sketch, "E11.25.0", {"start": v(9.36, -14.01) * mm, "end": v(9.4, -14.1) * mm});
            skLineSegment(sketch, "E11.25.1", {"start": v(9.4, -14.1) * mm, "end": v(9.51, -15.81) * mm});
            skLineSegment(sketch, "E11.25.2", {"start": v(9.23, -15.98) * mm, "end": v(9.51, -15.81) * mm});
            skLineSegment(sketch, "E11.25.3", {"start": v(9.23, -15.98) * mm, "end": v(8.94, -16.14) * mm});
            skLineSegment(sketch, "E11.25.4", {"start": v(7.5, -15.2) * mm, "end": v(8.94, -16.14) * mm});
            skLineSegment(sketch, "E11.25.5", {"start": v(7.45, -15.11) * mm, "end": v(7.5, -15.2) * mm});
            skLineSegment(sketch, "E11.26.0", {"start": v(12.07, -11.76) * mm, "end": v(12.14, -11.83) * mm});
            skLineSegment(sketch, "E11.26.1", {"start": v(12.14, -11.83) * mm, "end": v(12.6, -13.5) * mm});
            skLineSegment(sketch, "E11.26.2", {"start": v(12.35, -13.71) * mm, "end": v(12.6, -13.5) * mm});
            skLineSegment(sketch, "E11.26.3", {"start": v(12.35, -13.71) * mm, "end": v(12.1, -13.93) * mm});
            skLineSegment(sketch, "E11.26.4", {"start": v(10.5, -13.3) * mm, "end": v(12.1, -13.93) * mm});
            skLineSegment(sketch, "E11.26.5", {"start": v(10.43, -13.23) * mm, "end": v(10.5, -13.3) * mm});
            skLineSegment(sketch, "E11.27.0", {"start": v(14.25, -9) * mm, "end": v(14.33, -9.05) * mm});
            skLineSegment(sketch, "E11.27.1", {"start": v(14.33, -9.05) * mm, "end": v(15.12, -10.58) * mm});
            skLineSegment(sketch, "E11.27.2", {"start": v(14.93, -10.84) * mm, "end": v(15.12, -10.58) * mm});
            skLineSegment(sketch, "E11.27.3", {"start": v(14.93, -10.84) * mm, "end": v(14.73, -11.11) * mm});
            skLineSegment(sketch, "E11.27.4", {"start": v(13.04, -10.83) * mm, "end": v(14.73, -11.11) * mm});
            skLineSegment(sketch, "E11.27.5", {"start": v(12.96, -10.77) * mm, "end": v(13.04, -10.83) * mm});
            skLineSegment(sketch, "E11.28.0", {"start": v(15.8, -5.83) * mm, "end": v(15.9, -5.87) * mm});
            skLineSegment(sketch, "E11.28.1", {"start": v(15.9, -5.87) * mm, "end": v(16.99, -7.2) * mm});
            skLineSegment(sketch, "E11.28.2", {"start": v(16.85, -7.5) * mm, "end": v(16.99, -7.2) * mm});
            skLineSegment(sketch, "E11.28.3", {"start": v(16.85, -7.5) * mm, "end": v(16.72, -7.8) * mm});
            skLineSegment(sketch, "E11.28.4", {"start": v(15, -7.88) * mm, "end": v(16.72, -7.8) * mm});
            skLineSegment(sketch, "E11.28.5", {"start": v(14.91, -7.84) * mm, "end": v(15, -7.88) * mm});
            skLineSegment(sketch, "E11.29.0", {"start": v(16.68, -2.42) * mm, "end": v(16.77, -2.44) * mm});
            skLineSegment(sketch, "E11.29.1", {"start": v(16.77, -2.44) * mm, "end": v(18.12, -3.51) * mm});
            skLineSegment(sketch, "E11.29.2", {"start": v(18.05, -3.84) * mm, "end": v(18.12, -3.51) * mm});
            skLineSegment(sketch, "E11.29.3", {"start": v(18.05, -3.84) * mm, "end": v(17.98, -4.16) * mm});
            skLineSegment(sketch, "E11.29.4", {"start": v(16.32, -4.6) * mm, "end": v(17.98, -4.16) * mm});
            skLineSegment(sketch, "E11.29.5", {"start": v(16.22, -4.57) * mm, "end": v(16.32, -4.6) * mm});
            skSolve(sketch);
        }
        {
            var Q0;
            Q0=qSketchRegion(id+"F0",true);
            extrude(context, id + "F1", {"entities" : qUnion([Q0]), "depth" : 20 * mm, "offsetDistance" : 25.4 * mm});
        }
        {
            var Q0;
            Q0=makeQuery(id+"F1.opExtrude","CAP_FACE",FACE,{"disambiguationData":[OSD([sQuery(id+"F0.wireOp",EDGE,"E0"),sQuery(id+"F0.wireOp",EDGE,"E3"),sQuery(id+"F0.wireOp",EDGE,"E4"),sQuery(id+"F0.wireOp",EDGE,"E5"),sQuery(id+"F0.wireOp",EDGE,"E6.MirrorCS"),sQuery(id+"F0.wireOp",EDGE,"E7.MirrorCS"),sQuery(id+"F0.wireOp",EDGE,"E8.MirrorCS"),sQuery(id+"F0.wireOp",EDGE,"070828ce-9394-452a-aa16-b4793628ad7e.1.0"),sQuery(id+"F0.wireOp",EDGE,"070828ce-9394-452a-aa16-b4793628ad7e.1.1"),sQuery(id+"F0.wireOp",EDGE,"070828ce-9394-452a-aa16-b4793628ad7e.1.2"),sQuery(id+"F0.wireOp",EDGE,"070828ce-9394-452a-aa16-b4793628ad7e.1.3"),sQuery(id+"F0.wireOp",EDGE,"070828ce-9394-452a-aa16-b4793628ad7e.1.4"),sQuery(id+"F0.wireOp",EDGE,"070828ce-9394-452a-aa16-b4793628ad7e.1.5"),sQuery(id+"F0.wireOp",EDGE,"070828ce-9394-452a-aa16-b4793628ad7e.2.0"),sQuery(id+"F0.wireOp",EDGE,"070828ce-9394-452a-aa16-b4793628ad7e.2.1"),sQuery(id+"F0.wireOp",EDGE,"070828ce-9394-452a-aa16-b4793628ad7e.2.2"),sQuery(id+"F0.wireOp",EDGE,"070828ce-9394-452a-aa16-b4793628ad7e.2.3"),sQuery(id+"F0.wireOp",EDGE,"070828ce-9394-452a-aa16-b4793628ad7e.2.4"),sQuery(id+"F0.wireOp",EDGE,"070828ce-9394-452a-aa16-b4793628ad7e.2.5"),sQuery(id+"F0.wireOp",EDGE,"070828ce-9394-452a-aa16-b4793628ad7e.3.0"),sQuery(id+"F0.wireOp",EDGE,"070828ce-9394-452a-aa16-b4793628ad7e.3.1"),sQuery(id+"F0.wireOp",EDGE,"070828ce-9394-452a-aa16-b4793628ad7e.3.2"),sQuery(id+"F0.wireOp",EDGE,"070828ce-9394-452a-aa16-b4793628ad7e.3.3"),sQuery(id+"F0.wireOp",EDGE,"070828ce-9394-452a-aa16-b4793628ad7e.3.4"),sQuery(id+"F0.wireOp",EDGE,"070828ce-9394-452a-aa16-b4793628ad7e.3.5"),sQuery(id+"F0.wireOp",EDGE,"070828ce-9394-452a-aa16-b4793628ad7e.4.0"),sQuery(id+"F0.wireOp",EDGE,"070828ce-9394-452a-aa16-b4793628ad7e.4.1"),sQuery(id+"F0.wireOp",EDGE,"070828ce-9394-452a-aa16-b4793628ad7e.4.2"),sQuery(id+"F0.wireOp",EDGE,"070828ce-9394-452a-aa16-b4793628ad7e.4.3"),sQuery(id+"F0.wireOp",EDGE,"070828ce-9394-452a-aa16-b4793628ad7e.4.4"),sQuery(id+"F0.wireOp",EDGE,"070828ce-9394-452a-aa16-b4793628ad7e.4.5"),sQuery(id+"F0.wireOp",EDGE,"070828ce-9394-452a-aa16-b4793628ad7e.5.0"),sQuery(id+"F0.wireOp",EDGE,"070828ce-9394-452a-aa16-b4793628ad7e.5.1"),sQuery(id+"F0.wireOp",EDGE,"070828ce-9394-452a-aa16-b4793628ad7e.5.2"),sQuery(id+"F0.wireOp",EDGE,"070828ce-9394-452a-aa16-b4793628ad7e.5.3"),sQuery(id+"F0.wireOp",EDGE,"070828ce-9394-452a-aa16-b4793628ad7e.5.4"),sQuery(id+"F0.wireOp",EDGE,"070828ce-9394-452a-aa16-b4793628ad7e.5.5"),sQuery(id+"F0.wireOp",EDGE,"070828ce-9394-452a-aa16-b4793628ad7e.6.0"),sQuery(id+"F0.wireOp",EDGE,"070828ce-9394-452a-aa16-b4793628ad7e.6.1"),sQuery(id+"F0.wireOp",EDGE,"070828ce-9394-452a-aa16-b4793628ad7e.6.2"),sQuery(id+"F0.wireOp",EDGE,"070828ce-9394-452a-aa16-b4793628ad7e.6.3"),sQuery(id+"F0.wireOp",EDGE,"070828ce-9394-452a-aa16-b4793628ad7e.6.4"),sQuery(id+"F0.wireOp",EDGE,"070828ce-9394-452a-aa16-b4793628ad7e.6.5"),sQuery(id+"F0.wireOp",EDGE,"070828ce-9394-452a-aa16-b4793628ad7e.7.0"),sQuery(id+"F0.wireOp",EDGE,"070828ce-9394-452a-aa16-b4793628ad7e.7.1"),sQuery(id+"F0.wireOp",EDGE,"070828ce-9394-452a-aa16-b4793628ad7e.7.2"),sQuery(id+"F0.wireOp",EDGE,"070828ce-9394-452a-aa16-b4793628ad7e.7.3"),sQuery(id+"F0.wireOp",EDGE,"070828ce-9394-452a-aa16-b4793628ad7e.7.4"),sQuery(id+"F0.wireOp",EDGE,"070828ce-9394-452a-aa16-b4793628ad7e.7.5"),sQuery(id+"F0.wireOp",EDGE,"070828ce-9394-452a-aa16-b4793628ad7e.8.0"),sQuery(id+"F0.wireOp",EDGE,"070828ce-9394-452a-aa16-b4793628ad7e.8.1"),sQuery(id+"F0.wireOp",EDGE,"070828ce-9394-452a-aa16-b4793628ad7e.8.2"),sQuery(id+"F0.wireOp",EDGE,"070828ce-9394-452a-aa16-b4793628ad7e.8.3"),sQuery(id+"F0.wireOp",EDGE,"070828ce-9394-452a-aa16-b4793628ad7e.8.4"),sQuery(id+"F0.wireOp",EDGE,"070828ce-9394-452a-aa16-b4793628ad7e.8.5"),sQuery(id+"F0.wireOp",EDGE,"070828ce-9394-452a-aa16-b4793628ad7e.9.0"),sQuery(id+"F0.wireOp",EDGE,"070828ce-9394-452a-aa16-b4793628ad7e.9.1"),sQuery(id+"F0.wireOp",EDGE,"070828ce-9394-452a-aa16-b4793628ad7e.9.2"),sQuery(id+"F0.wireOp",EDGE,"070828ce-9394-452a-aa16-b4793628ad7e.9.3"),sQuery(id+"F0.wireOp",EDGE,"070828ce-9394-452a-aa16-b4793628ad7e.9.4"),sQuery(id+"F0.wireOp",EDGE,"070828ce-9394-452a-aa16-b4793628ad7e.9.5"),sQuery(id+"F0.wireOp",EDGE,"070828ce-9394-452a-aa16-b4793628ad7e.10.0"),sQuery(id+"F0.wireOp",EDGE,"070828ce-9394-452a-aa16-b4793628ad7e.10.1"),sQuery(id+"F0.wireOp",EDGE,"070828ce-9394-452a-aa16-b4793628ad7e.10.2"),sQuery(id+"F0.wireOp",EDGE,"070828ce-9394-452a-aa16-b4793628ad7e.10.3"),sQuery(id+"F0.wireOp",EDGE,"070828ce-9394-452a-aa16-b4793628ad7e.10.4"),sQuery(id+"F0.wireOp",EDGE,"070828ce-9394-452a-aa16-b4793628ad7e.10.5"),sQuery(id+"F0.wireOp",EDGE,"070828ce-9394-452a-aa16-b4793628ad7e.11.0"),sQuery(id+"F0.wireOp",EDGE,"070828ce-9394-452a-aa16-b4793628ad7e.11.1"),sQuery(id+"F0.wireOp",EDGE,"070828ce-9394-452a-aa16-b4793628ad7e.11.2"),sQuery(id+"F0.wireOp",EDGE,"070828ce-9394-452a-aa16-b4793628ad7e.11.3"),sQuery(id+"F0.wireOp",EDGE,"070828ce-9394-452a-aa16-b4793628ad7e.11.4"),sQuery(id+"F0.wireOp",EDGE,"070828ce-9394-452a-aa16-b4793628ad7e.11.5"),sQuery(id+"F0.wireOp",EDGE,"070828ce-9394-452a-aa16-b4793628ad7e.12.0"),sQuery(id+"F0.wireOp",EDGE,"070828ce-9394-452a-aa16-b4793628ad7e.12.1"),sQuery(id+"F0.wireOp",EDGE,"070828ce-9394-452a-aa16-b4793628ad7e.12.2"),sQuery(id+"F0.wireOp",EDGE,"070828ce-9394-452a-aa16-b4793628ad7e.12.3"),sQuery(id+"F0.wireOp",EDGE,"070828ce-9394-452a-aa16-b4793628ad7e.12.4"),sQuery(id+"F0.wireOp",EDGE,"070828ce-9394-452a-aa16-b4793628ad7e.12.5"),sQuery(id+"F0.wireOp",EDGE,"070828ce-9394-452a-aa16-b4793628ad7e.13.0"),sQuery(id+"F0.wireOp",EDGE,"070828ce-9394-452a-aa16-b4793628ad7e.13.1"),sQuery(id+"F0.wireOp",EDGE,"070828ce-9394-452a-aa16-b4793628ad7e.13.2"),sQuery(id+"F0.wireOp",EDGE,"070828ce-9394-452a-aa16-b4793628ad7e.13.3"),sQuery(id+"F0.wireOp",EDGE,"070828ce-9394-452a-aa16-b4793628ad7e.13.4"),sQuery(id+"F0.wireOp",EDGE,"070828ce-9394-452a-aa16-b4793628ad7e.13.5"),sQuery(id+"F0.wireOp",EDGE,"070828ce-9394-452a-aa16-b4793628ad7e.14.0"),sQuery(id+"F0.wireOp",EDGE,"070828ce-9394-452a-aa16-b4793628ad7e.14.1"),sQuery(id+"F0.wireOp",EDGE,"070828ce-9394-452a-aa16-b4793628ad7e.14.2"),sQuery(id+"F0.wireOp",EDGE,"070828ce-9394-452a-aa16-b4793628ad7e.14.3"),sQuery(id+"F0.wireOp",EDGE,"070828ce-9394-452a-aa16-b4793628ad7e.14.4"),sQuery(id+"F0.wireOp",EDGE,"070828ce-9394-452a-aa16-b4793628ad7e.14.5"),sQuery(id+"F0.wireOp",EDGE,"070828ce-9394-452a-aa16-b4793628ad7e.15.0"),sQuery(id+"F0.wireOp",EDGE,"070828ce-9394-452a-aa16-b4793628ad7e.15.1"),sQuery(id+"F0.wireOp",EDGE,"070828ce-9394-452a-aa16-b4793628ad7e.15.2"),sQuery(id+"F0.wireOp",EDGE,"070828ce-9394-452a-aa16-b4793628ad7e.15.3"),sQuery(id+"F0.wireOp",EDGE,"070828ce-9394-452a-aa16-b4793628ad7e.15.4"),sQuery(id+"F0.wireOp",EDGE,"070828ce-9394-452a-aa16-b4793628ad7e.15.5"),sQuery(id+"F0.wireOp",EDGE,"070828ce-9394-452a-aa16-b4793628ad7e.16.0"),sQuery(id+"F0.wireOp",EDGE,"070828ce-9394-452a-aa16-b4793628ad7e.16.1"),sQuery(id+"F0.wireOp",EDGE,"070828ce-9394-452a-aa16-b4793628ad7e.16.2"),sQuery(id+"F0.wireOp",EDGE,"070828ce-9394-452a-aa16-b4793628ad7e.16.3"),sQuery(id+"F0.wireOp",EDGE,"070828ce-9394-452a-aa16-b4793628ad7e.16.4"),sQuery(id+"F0.wireOp",EDGE,"070828ce-9394-452a-aa16-b4793628ad7e.16.5"),sQuery(id+"F0.wireOp",EDGE,"070828ce-9394-452a-aa16-b4793628ad7e.17.0"),sQuery(id+"F0.wireOp",EDGE,"070828ce-9394-452a-aa16-b4793628ad7e.17.1"),sQuery(id+"F0.wireOp",EDGE,"070828ce-9394-452a-aa16-b4793628ad7e.17.2"),sQuery(id+"F0.wireOp",EDGE,"070828ce-9394-452a-aa16-b4793628ad7e.17.3"),sQuery(id+"F0.wireOp",EDGE,"070828ce-9394-452a-aa16-b4793628ad7e.17.4"),sQuery(id+"F0.wireOp",EDGE,"070828ce-9394-452a-aa16-b4793628ad7e.17.5"),sQuery(id+"F0.wireOp",EDGE,"070828ce-9394-452a-aa16-b4793628ad7e.18.0"),sQuery(id+"F0.wireOp",EDGE,"070828ce-9394-452a-aa16-b4793628ad7e.18.1"),sQuery(id+"F0.wireOp",EDGE,"070828ce-9394-452a-aa16-b4793628ad7e.18.2"),sQuery(id+"F0.wireOp",EDGE,"070828ce-9394-452a-aa16-b4793628ad7e.18.3"),sQuery(id+"F0.wireOp",EDGE,"070828ce-9394-452a-aa16-b4793628ad7e.18.4"),sQuery(id+"F0.wireOp",EDGE,"070828ce-9394-452a-aa16-b4793628ad7e.18.5"),sQuery(id+"F0.wireOp",EDGE,"070828ce-9394-452a-aa16-b4793628ad7e.19.0"),sQuery(id+"F0.wireOp",EDGE,"070828ce-9394-452a-aa16-b4793628ad7e.19.1"),sQuery(id+"F0.wireOp",EDGE,"070828ce-9394-452a-aa16-b4793628ad7e.19.2"),sQuery(id+"F0.wireOp",EDGE,"070828ce-9394-452a-aa16-b4793628ad7e.19.3"),sQuery(id+"F0.wireOp",EDGE,"070828ce-9394-452a-aa16-b4793628ad7e.19.4"),sQuery(id+"F0.wireOp",EDGE,"070828ce-9394-452a-aa16-b4793628ad7e.19.5"),sQuery(id+"F0.wireOp",EDGE,"070828ce-9394-452a-aa16-b4793628ad7e.20.0"),sQuery(id+"F0.wireOp",EDGE,"070828ce-9394-452a-aa16-b4793628ad7e.20.1"),sQuery(id+"F0.wireOp",EDGE,"070828ce-9394-452a-aa16-b4793628ad7e.20.2"),sQuery(id+"F0.wireOp",EDGE,"070828ce-9394-452a-aa16-b4793628ad7e.20.3"),sQuery(id+"F0.wireOp",EDGE,"070828ce-9394-452a-aa16-b4793628ad7e.20.4"),sQuery(id+"F0.wireOp",EDGE,"070828ce-9394-452a-aa16-b4793628ad7e.20.5"),sQuery(id+"F0.wireOp",EDGE,"070828ce-9394-452a-aa16-b4793628ad7e.21.0"),sQuery(id+"F0.wireOp",EDGE,"070828ce-9394-452a-aa16-b4793628ad7e.21.1"),sQuery(id+"F0.wireOp",EDGE,"070828ce-9394-452a-aa16-b4793628ad7e.21.2"),sQuery(id+"F0.wireOp",EDGE,"070828ce-9394-452a-aa16-b4793628ad7e.21.3"),sQuery(id+"F0.wireOp",EDGE,"070828ce-9394-452a-aa16-b4793628ad7e.21.4"),sQuery(id+"F0.wireOp",EDGE,"070828ce-9394-452a-aa16-b4793628ad7e.21.5"),sQuery(id+"F0.wireOp",EDGE,"070828ce-9394-452a-aa16-b4793628ad7e.22.0"),sQuery(id+"F0.wireOp",EDGE,"070828ce-9394-452a-aa16-b4793628ad7e.22.1"),sQuery(id+"F0.wireOp",EDGE,"070828ce-9394-452a-aa16-b4793628ad7e.22.2"),sQuery(id+"F0.wireOp",EDGE,"070828ce-9394-452a-aa16-b4793628ad7e.22.3"),sQuery(id+"F0.wireOp",EDGE,"070828ce-9394-452a-aa16-b4793628ad7e.22.4"),sQuery(id+"F0.wireOp",EDGE,"070828ce-9394-452a-aa16-b4793628ad7e.22.5"),sQuery(id+"F0.wireOp",EDGE,"070828ce-9394-452a-aa16-b4793628ad7e.23.0"),sQuery(id+"F0.wireOp",EDGE,"070828ce-9394-452a-aa16-b4793628ad7e.23.1"),sQuery(id+"F0.wireOp",EDGE,"070828ce-9394-452a-aa16-b4793628ad7e.23.2"),sQuery(id+"F0.wireOp",EDGE,"070828ce-9394-452a-aa16-b4793628ad7e.23.3"),sQuery(id+"F0.wireOp",EDGE,"070828ce-9394-452a-aa16-b4793628ad7e.23.4"),sQuery(id+"F0.wireOp",EDGE,"070828ce-9394-452a-aa16-b4793628ad7e.23.5"),sQuery(id+"F0.wireOp",EDGE,"070828ce-9394-452a-aa16-b4793628ad7e.24.0"),sQuery(id+"F0.wireOp",EDGE,"070828ce-9394-452a-aa16-b4793628ad7e.24.1"),sQuery(id+"F0.wireOp",EDGE,"070828ce-9394-452a-aa16-b4793628ad7e.24.2"),sQuery(id+"F0.wireOp",EDGE,"070828ce-9394-452a-aa16-b4793628ad7e.24.3"),sQuery(id+"F0.wireOp",EDGE,"070828ce-9394-452a-aa16-b4793628ad7e.24.4"),sQuery(id+"F0.wireOp",EDGE,"070828ce-9394-452a-aa16-b4793628ad7e.24.5"),sQuery(id+"F0.wireOp",EDGE,"070828ce-9394-452a-aa16-b4793628ad7e.25.0"),sQuery(id+"F0.wireOp",EDGE,"070828ce-9394-452a-aa16-b4793628ad7e.25.1"),sQuery(id+"F0.wireOp",EDGE,"070828ce-9394-452a-aa16-b4793628ad7e.25.2"),sQuery(id+"F0.wireOp",EDGE,"070828ce-9394-452a-aa16-b4793628ad7e.25.3"),sQuery(id+"F0.wireOp",EDGE,"070828ce-9394-452a-aa16-b4793628ad7e.25.4"),sQuery(id+"F0.wireOp",EDGE,"070828ce-9394-452a-aa16-b4793628ad7e.25.5"),sQuery(id+"F0.wireOp",EDGE,"070828ce-9394-452a-aa16-b4793628ad7e.26.0"),sQuery(id+"F0.wireOp",EDGE,"070828ce-9394-452a-aa16-b4793628ad7e.26.1"),sQuery(id+"F0.wireOp",EDGE,"070828ce-9394-452a-aa16-b4793628ad7e.26.2"),sQuery(id+"F0.wireOp",EDGE,"070828ce-9394-452a-aa16-b4793628ad7e.26.3"),sQuery(id+"F0.wireOp",EDGE,"070828ce-9394-452a-aa16-b4793628ad7e.26.4"),sQuery(id+"F0.wireOp",EDGE,"070828ce-9394-452a-aa16-b4793628ad7e.26.5"),sQuery(id+"F0.wireOp",EDGE,"070828ce-9394-452a-aa16-b4793628ad7e.27.0"),sQuery(id+"F0.wireOp",EDGE,"070828ce-9394-452a-aa16-b4793628ad7e.27.1"),sQuery(id+"F0.wireOp",EDGE,"070828ce-9394-452a-aa16-b4793628ad7e.27.2"),sQuery(id+"F0.wireOp",EDGE,"070828ce-9394-452a-aa16-b4793628ad7e.27.3"),sQuery(id+"F0.wireOp",EDGE,"070828ce-9394-452a-aa16-b4793628ad7e.27.4"),sQuery(id+"F0.wireOp",EDGE,"070828ce-9394-452a-aa16-b4793628ad7e.27.5"),sQuery(id+"F0.wireOp",EDGE,"070828ce-9394-452a-aa16-b4793628ad7e.28.0"),sQuery(id+"F0.wireOp",EDGE,"070828ce-9394-452a-aa16-b4793628ad7e.28.1"),sQuery(id+"F0.wireOp",EDGE,"070828ce-9394-452a-aa16-b4793628ad7e.28.2"),sQuery(id+"F0.wireOp",EDGE,"070828ce-9394-452a-aa16-b4793628ad7e.28.3"),sQuery(id+"F0.wireOp",EDGE,"070828ce-9394-452a-aa16-b4793628ad7e.28.4"),sQuery(id+"F0.wireOp",EDGE,"070828ce-9394-452a-aa16-b4793628ad7e.28.5"),sQuery(id+"F0.wireOp",EDGE,"070828ce-9394-452a-aa16-b4793628ad7e.29.0"),sQuery(id+"F0.wireOp",EDGE,"070828ce-9394-452a-aa16-b4793628ad7e.29.1"),sQuery(id+"F0.wireOp",EDGE,"070828ce-9394-452a-aa16-b4793628ad7e.29.2"),sQuery(id+"F0.wireOp",EDGE,"070828ce-9394-452a-aa16-b4793628ad7e.29.3"),sQuery(id+"F0.wireOp",EDGE,"070828ce-9394-452a-aa16-b4793628ad7e.29.4"),sQuery(id+"F0.wireOp",EDGE,"070828ce-9394-452a-aa16-b4793628ad7e.29.5"),sQuery(id+"F0.wireOp",EDGE,"070828ce-9394-452a-aa16-b4793628ad7e.30.0"),sQuery(id+"F0.wireOp",EDGE,"070828ce-9394-452a-aa16-b4793628ad7e.30.1"),sQuery(id+"F0.wireOp",EDGE,"070828ce-9394-452a-aa16-b4793628ad7e.30.2"),sQuery(id+"F0.wireOp",EDGE,"070828ce-9394-452a-aa16-b4793628ad7e.30.3"),sQuery(id+"F0.wireOp",EDGE,"070828ce-9394-452a-aa16-b4793628ad7e.30.4"),sQuery(id+"F0.wireOp",EDGE,"070828ce-9394-452a-aa16-b4793628ad7e.30.5"),sQuery(id+"F0.wireOp",EDGE,"070828ce-9394-452a-aa16-b4793628ad7e.31.0"),sQuery(id+"F0.wireOp",EDGE,"070828ce-9394-452a-aa16-b4793628ad7e.31.1"),sQuery(id+"F0.wireOp",EDGE,"070828ce-9394-452a-aa16-b4793628ad7e.31.2"),sQuery(id+"F0.wireOp",EDGE,"070828ce-9394-452a-aa16-b4793628ad7e.31.3"),sQuery(id+"F0.wireOp",EDGE,"070828ce-9394-452a-aa16-b4793628ad7e.31.4"),sQuery(id+"F0.wireOp",EDGE,"070828ce-9394-452a-aa16-b4793628ad7e.31.5"),sQuery(id+"F0.wireOp",EDGE,"070828ce-9394-452a-aa16-b4793628ad7e.32.0"),sQuery(id+"F0.wireOp",EDGE,"070828ce-9394-452a-aa16-b4793628ad7e.32.1"),sQuery(id+"F0.wireOp",EDGE,"070828ce-9394-452a-aa16-b4793628ad7e.32.2"),sQuery(id+"F0.wireOp",EDGE,"070828ce-9394-452a-aa16-b4793628ad7e.32.3"),sQuery(id+"F0.wireOp",EDGE,"070828ce-9394-452a-aa16-b4793628ad7e.32.4"),sQuery(id+"F0.wireOp",EDGE,"070828ce-9394-452a-aa16-b4793628ad7e.32.5"),sQuery(id+"F0.wireOp",EDGE,"070828ce-9394-452a-aa16-b4793628ad7e.33.0"),sQuery(id+"F0.wireOp",EDGE,"070828ce-9394-452a-aa16-b4793628ad7e.33.1"),sQuery(id+"F0.wireOp",EDGE,"070828ce-9394-452a-aa16-b4793628ad7e.33.2"),sQuery(id+"F0.wireOp",EDGE,"070828ce-9394-452a-aa16-b4793628ad7e.33.3"),sQuery(id+"F0.wireOp",EDGE,"070828ce-9394-452a-aa16-b4793628ad7e.33.4"),sQuery(id+"F0.wireOp",EDGE,"070828ce-9394-452a-aa16-b4793628ad7e.33.5"),sQuery(id+"F0.wireOp",EDGE,"070828ce-9394-452a-aa16-b4793628ad7e.34.0"),sQuery(id+"F0.wireOp",EDGE,"070828ce-9394-452a-aa16-b4793628ad7e.34.1"),sQuery(id+"F0.wireOp",EDGE,"070828ce-9394-452a-aa16-b4793628ad7e.34.2"),sQuery(id+"F0.wireOp",EDGE,"070828ce-9394-452a-aa16-b4793628ad7e.34.3"),sQuery(id+"F0.wireOp",EDGE,"070828ce-9394-452a-aa16-b4793628ad7e.34.4"),sQuery(id+"F0.wireOp",EDGE,"070828ce-9394-452a-aa16-b4793628ad7e.34.5"),sQuery(id+"F0.wireOp",EDGE,"070828ce-9394-452a-aa16-b4793628ad7e.35.0"),sQuery(id+"F0.wireOp",EDGE,"070828ce-9394-452a-aa16-b4793628ad7e.35.1"),sQuery(id+"F0.wireOp",EDGE,"070828ce-9394-452a-aa16-b4793628ad7e.35.2"),sQuery(id+"F0.wireOp",EDGE,"070828ce-9394-452a-aa16-b4793628ad7e.35.3"),sQuery(id+"F0.wireOp",EDGE,"070828ce-9394-452a-aa16-b4793628ad7e.35.4"),sQuery(id+"F0.wireOp",EDGE,"070828ce-9394-452a-aa16-b4793628ad7e.35.5"),sQuery(id+"F0.wireOp",EDGE,"070828ce-9394-452a-aa16-b4793628ad7e.36.0"),sQuery(id+"F0.wireOp",EDGE,"070828ce-9394-452a-aa16-b4793628ad7e.36.1"),sQuery(id+"F0.wireOp",EDGE,"070828ce-9394-452a-aa16-b4793628ad7e.36.2"),sQuery(id+"F0.wireOp",EDGE,"070828ce-9394-452a-aa16-b4793628ad7e.36.3"),sQuery(id+"F0.wireOp",EDGE,"070828ce-9394-452a-aa16-b4793628ad7e.36.4"),sQuery(id+"F0.wireOp",EDGE,"070828ce-9394-452a-aa16-b4793628ad7e.36.5"),sQuery(id+"F0.wireOp",EDGE,"070828ce-9394-452a-aa16-b4793628ad7e.37.0"),sQuery(id+"F0.wireOp",EDGE,"070828ce-9394-452a-aa16-b4793628ad7e.37.1"),sQuery(id+"F0.wireOp",EDGE,"070828ce-9394-452a-aa16-b4793628ad7e.37.2"),sQuery(id+"F0.wireOp",EDGE,"070828ce-9394-452a-aa16-b4793628ad7e.37.3"),sQuery(id+"F0.wireOp",EDGE,"070828ce-9394-452a-aa16-b4793628ad7e.37.4"),sQuery(id+"F0.wireOp",EDGE,"070828ce-9394-452a-aa16-b4793628ad7e.37.5"),sQuery(id+"F0.wireOp",EDGE,"070828ce-9394-452a-aa16-b4793628ad7e.38.0"),sQuery(id+"F0.wireOp",EDGE,"070828ce-9394-452a-aa16-b4793628ad7e.38.1"),sQuery(id+"F0.wireOp",EDGE,"070828ce-9394-452a-aa16-b4793628ad7e.38.2"),sQuery(id+"F0.wireOp",EDGE,"070828ce-9394-452a-aa16-b4793628ad7e.38.3"),sQuery(id+"F0.wireOp",EDGE,"070828ce-9394-452a-aa16-b4793628ad7e.38.4"),sQuery(id+"F0.wireOp",EDGE,"070828ce-9394-452a-aa16-b4793628ad7e.38.5"),sQuery(id+"F0.wireOp",EDGE,"070828ce-9394-452a-aa16-b4793628ad7e.39.0"),sQuery(id+"F0.wireOp",EDGE,"070828ce-9394-452a-aa16-b4793628ad7e.39.1"),sQuery(id+"F0.wireOp",EDGE,"070828ce-9394-452a-aa16-b4793628ad7e.39.2"),sQuery(id+"F0.wireOp",EDGE,"070828ce-9394-452a-aa16-b4793628ad7e.39.3"),sQuery(id+"F0.wireOp",EDGE,"070828ce-9394-452a-aa16-b4793628ad7e.39.4"),sQuery(id+"F0.wireOp",EDGE,"070828ce-9394-452a-aa16-b4793628ad7e.39.5"),sQuery(id+"F0.wireOp",EDGE,"070828ce-9394-452a-aa16-b4793628ad7e.40.0"),sQuery(id+"F0.wireOp",EDGE,"070828ce-9394-452a-aa16-b4793628ad7e.40.1"),sQuery(id+"F0.wireOp",EDGE,"070828ce-9394-452a-aa16-b4793628ad7e.40.2"),sQuery(id+"F0.wireOp",EDGE,"070828ce-9394-452a-aa16-b4793628ad7e.40.3"),sQuery(id+"F0.wireOp",EDGE,"070828ce-9394-452a-aa16-b4793628ad7e.40.4"),sQuery(id+"F0.wireOp",EDGE,"070828ce-9394-452a-aa16-b4793628ad7e.40.5"),sQuery(id+"F0.wireOp",EDGE,"070828ce-9394-452a-aa16-b4793628ad7e.41.0"),sQuery(id+"F0.wireOp",EDGE,"070828ce-9394-452a-aa16-b4793628ad7e.41.1"),sQuery(id+"F0.wireOp",EDGE,"070828ce-9394-452a-aa16-b4793628ad7e.41.2"),sQuery(id+"F0.wireOp",EDGE,"070828ce-9394-452a-aa16-b4793628ad7e.41.3"),sQuery(id+"F0.wireOp",EDGE,"070828ce-9394-452a-aa16-b4793628ad7e.41.4"),sQuery(id+"F0.wireOp",EDGE,"070828ce-9394-452a-aa16-b4793628ad7e.41.5"),sQuery(id+"F0.wireOp",EDGE,"070828ce-9394-452a-aa16-b4793628ad7e.42.0"),sQuery(id+"F0.wireOp",EDGE,"070828ce-9394-452a-aa16-b4793628ad7e.42.1"),sQuery(id+"F0.wireOp",EDGE,"070828ce-9394-452a-aa16-b4793628ad7e.42.2"),sQuery(id+"F0.wireOp",EDGE,"070828ce-9394-452a-aa16-b4793628ad7e.42.3"),sQuery(id+"F0.wireOp",EDGE,"070828ce-9394-452a-aa16-b4793628ad7e.42.4"),sQuery(id+"F0.wireOp",EDGE,"070828ce-9394-452a-aa16-b4793628ad7e.42.5"),sQuery(id+"F0.wireOp",EDGE,"070828ce-9394-452a-aa16-b4793628ad7e.43.0"),sQuery(id+"F0.wireOp",EDGE,"070828ce-9394-452a-aa16-b4793628ad7e.43.1"),sQuery(id+"F0.wireOp",EDGE,"070828ce-9394-452a-aa16-b4793628ad7e.43.2"),sQuery(id+"F0.wireOp",EDGE,"070828ce-9394-452a-aa16-b4793628ad7e.43.3"),sQuery(id+"F0.wireOp",EDGE,"070828ce-9394-452a-aa16-b4793628ad7e.43.4"),sQuery(id+"F0.wireOp",EDGE,"070828ce-9394-452a-aa16-b4793628ad7e.43.5"),sQuery(id+"F0.wireOp",EDGE,"070828ce-9394-452a-aa16-b4793628ad7e.44.0"),sQuery(id+"F0.wireOp",EDGE,"070828ce-9394-452a-aa16-b4793628ad7e.44.1"),sQuery(id+"F0.wireOp",EDGE,"070828ce-9394-452a-aa16-b4793628ad7e.44.2"),sQuery(id+"F0.wireOp",EDGE,"070828ce-9394-452a-aa16-b4793628ad7e.44.3"),sQuery(id+"F0.wireOp",EDGE,"070828ce-9394-452a-aa16-b4793628ad7e.44.4"),sQuery(id+"F0.wireOp",EDGE,"070828ce-9394-452a-aa16-b4793628ad7e.44.5"),sQuery(id+"F0.wireOp",EDGE,"070828ce-9394-452a-aa16-b4793628ad7e.45.0"),sQuery(id+"F0.wireOp",EDGE,"070828ce-9394-452a-aa16-b4793628ad7e.45.1"),sQuery(id+"F0.wireOp",EDGE,"070828ce-9394-452a-aa16-b4793628ad7e.45.2"),sQuery(id+"F0.wireOp",EDGE,"070828ce-9394-452a-aa16-b4793628ad7e.45.3"),sQuery(id+"F0.wireOp",EDGE,"070828ce-9394-452a-aa16-b4793628ad7e.45.4"),sQuery(id+"F0.wireOp",EDGE,"070828ce-9394-452a-aa16-b4793628ad7e.45.5"),sQuery(id+"F0.wireOp",EDGE,"070828ce-9394-452a-aa16-b4793628ad7e.46.0"),sQuery(id+"F0.wireOp",EDGE,"070828ce-9394-452a-aa16-b4793628ad7e.46.1"),sQuery(id+"F0.wireOp",EDGE,"070828ce-9394-452a-aa16-b4793628ad7e.46.2"),sQuery(id+"F0.wireOp",EDGE,"070828ce-9394-452a-aa16-b4793628ad7e.46.3"),sQuery(id+"F0.wireOp",EDGE,"070828ce-9394-452a-aa16-b4793628ad7e.46.4"),sQuery(id+"F0.wireOp",EDGE,"070828ce-9394-452a-aa16-b4793628ad7e.46.5"),sQuery(id+"F0.wireOp",EDGE,"070828ce-9394-452a-aa16-b4793628ad7e.47.0"),sQuery(id+"F0.wireOp",EDGE,"070828ce-9394-452a-aa16-b4793628ad7e.47.1"),sQuery(id+"F0.wireOp",EDGE,"070828ce-9394-452a-aa16-b4793628ad7e.47.2"),sQuery(id+"F0.wireOp",EDGE,"070828ce-9394-452a-aa16-b4793628ad7e.47.3"),sQuery(id+"F0.wireOp",EDGE,"070828ce-9394-452a-aa16-b4793628ad7e.47.4"),sQuery(id+"F0.wireOp",EDGE,"070828ce-9394-452a-aa16-b4793628ad7e.47.5"),sQuery(id+"F0.wireOp",EDGE,"070828ce-9394-452a-aa16-b4793628ad7e.48.0"),sQuery(id+"F0.wireOp",EDGE,"070828ce-9394-452a-aa16-b4793628ad7e.48.1"),sQuery(id+"F0.wireOp",EDGE,"070828ce-9394-452a-aa16-b4793628ad7e.48.2"),sQuery(id+"F0.wireOp",EDGE,"070828ce-9394-452a-aa16-b4793628ad7e.48.3"),sQuery(id+"F0.wireOp",EDGE,"070828ce-9394-452a-aa16-b4793628ad7e.48.4"),sQuery(id+"F0.wireOp",EDGE,"070828ce-9394-452a-aa16-b4793628ad7e.48.5"),sQuery(id+"F0.wireOp",EDGE,"070828ce-9394-452a-aa16-b4793628ad7e.49.0"),sQuery(id+"F0.wireOp",EDGE,"070828ce-9394-452a-aa16-b4793628ad7e.49.1"),sQuery(id+"F0.wireOp",EDGE,"070828ce-9394-452a-aa16-b4793628ad7e.49.2"),sQuery(id+"F0.wireOp",EDGE,"070828ce-9394-452a-aa16-b4793628ad7e.49.3"),sQuery(id+"F0.wireOp",EDGE,"070828ce-9394-452a-aa16-b4793628ad7e.49.4"),sQuery(id+"F0.wireOp",EDGE,"070828ce-9394-452a-aa16-b4793628ad7e.49.5"),sQuery(id+"F0.wireOp",EDGE,"070828ce-9394-452a-aa16-b4793628ad7e.50.0"),sQuery(id+"F0.wireOp",EDGE,"070828ce-9394-452a-aa16-b4793628ad7e.50.1"),sQuery(id+"F0.wireOp",EDGE,"070828ce-9394-452a-aa16-b4793628ad7e.50.2"),sQuery(id+"F0.wireOp",EDGE,"070828ce-9394-452a-aa16-b4793628ad7e.50.3"),sQuery(id+"F0.wireOp",EDGE,"070828ce-9394-452a-aa16-b4793628ad7e.50.4"),sQuery(id+"F0.wireOp",EDGE,"070828ce-9394-452a-aa16-b4793628ad7e.50.5"),sQuery(id+"F0.wireOp",EDGE,"070828ce-9394-452a-aa16-b4793628ad7e.51.0"),sQuery(id+"F0.wireOp",EDGE,"070828ce-9394-452a-aa16-b4793628ad7e.51.1"),sQuery(id+"F0.wireOp",EDGE,"070828ce-9394-452a-aa16-b4793628ad7e.51.2"),sQuery(id+"F0.wireOp",EDGE,"070828ce-9394-452a-aa16-b4793628ad7e.51.3"),sQuery(id+"F0.wireOp",EDGE,"070828ce-9394-452a-aa16-b4793628ad7e.51.4"),sQuery(id+"F0.wireOp",EDGE,"070828ce-9394-452a-aa16-b4793628ad7e.51.5"),sQuery(id+"F0.wireOp",EDGE,"070828ce-9394-452a-aa16-b4793628ad7e.52.0"),sQuery(id+"F0.wireOp",EDGE,"070828ce-9394-452a-aa16-b4793628ad7e.52.1"),sQuery(id+"F0.wireOp",EDGE,"070828ce-9394-452a-aa16-b4793628ad7e.52.2"),sQuery(id+"F0.wireOp",EDGE,"070828ce-9394-452a-aa16-b4793628ad7e.52.3"),sQuery(id+"F0.wireOp",EDGE,"070828ce-9394-452a-aa16-b4793628ad7e.52.4"),sQuery(id+"F0.wireOp",EDGE,"070828ce-9394-452a-aa16-b4793628ad7e.52.5"),sQuery(id+"F0.wireOp",EDGE,"070828ce-9394-452a-aa16-b4793628ad7e.53.0"),sQuery(id+"F0.wireOp",EDGE,"070828ce-9394-452a-aa16-b4793628ad7e.53.1"),sQuery(id+"F0.wireOp",EDGE,"070828ce-9394-452a-aa16-b4793628ad7e.53.2"),sQuery(id+"F0.wireOp",EDGE,"070828ce-9394-452a-aa16-b4793628ad7e.53.3"),sQuery(id+"F0.wireOp",EDGE,"070828ce-9394-452a-aa16-b4793628ad7e.53.4"),sQuery(id+"F0.wireOp",EDGE,"070828ce-9394-452a-aa16-b4793628ad7e.53.5"),sQuery(id+"F0.wireOp",EDGE,"070828ce-9394-452a-aa16-b4793628ad7e.54.0"),sQuery(id+"F0.wireOp",EDGE,"070828ce-9394-452a-aa16-b4793628ad7e.54.1"),sQuery(id+"F0.wireOp",EDGE,"070828ce-9394-452a-aa16-b4793628ad7e.54.2"),sQuery(id+"F0.wireOp",EDGE,"070828ce-9394-452a-aa16-b4793628ad7e.54.3"),sQuery(id+"F0.wireOp",EDGE,"070828ce-9394-452a-aa16-b4793628ad7e.54.4"),sQuery(id+"F0.wireOp",EDGE,"070828ce-9394-452a-aa16-b4793628ad7e.54.5"),sQuery(id+"F0.wireOp",EDGE,"070828ce-9394-452a-aa16-b4793628ad7e.55.0"),sQuery(id+"F0.wireOp",EDGE,"070828ce-9394-452a-aa16-b4793628ad7e.55.1"),sQuery(id+"F0.wireOp",EDGE,"070828ce-9394-452a-aa16-b4793628ad7e.55.2"),sQuery(id+"F0.wireOp",EDGE,"070828ce-9394-452a-aa16-b4793628ad7e.55.3"),sQuery(id+"F0.wireOp",EDGE,"070828ce-9394-452a-aa16-b4793628ad7e.55.4"),sQuery(id+"F0.wireOp",EDGE,"070828ce-9394-452a-aa16-b4793628ad7e.55.5"),sQuery(id+"F0.wireOp",EDGE,"070828ce-9394-452a-aa16-b4793628ad7e.56.0"),sQuery(id+"F0.wireOp",EDGE,"070828ce-9394-452a-aa16-b4793628ad7e.56.1"),sQuery(id+"F0.wireOp",EDGE,"070828ce-9394-452a-aa16-b4793628ad7e.56.2"),sQuery(id+"F0.wireOp",EDGE,"070828ce-9394-452a-aa16-b4793628ad7e.56.3"),sQuery(id+"F0.wireOp",EDGE,"070828ce-9394-452a-aa16-b4793628ad7e.56.4"),sQuery(id+"F0.wireOp",EDGE,"070828ce-9394-452a-aa16-b4793628ad7e.56.5"),sQuery(id+"F0.wireOp",EDGE,"070828ce-9394-452a-aa16-b4793628ad7e.57.0"),sQuery(id+"F0.wireOp",EDGE,"070828ce-9394-452a-aa16-b4793628ad7e.57.1"),sQuery(id+"F0.wireOp",EDGE,"070828ce-9394-452a-aa16-b4793628ad7e.57.2"),sQuery(id+"F0.wireOp",EDGE,"070828ce-9394-452a-aa16-b4793628ad7e.57.3"),sQuery(id+"F0.wireOp",EDGE,"070828ce-9394-452a-aa16-b4793628ad7e.57.4"),sQuery(id+"F0.wireOp",EDGE,"070828ce-9394-452a-aa16-b4793628ad7e.57.5"),sQuery(id+"F0.wireOp",EDGE,"070828ce-9394-452a-aa16-b4793628ad7e.58.0"),sQuery(id+"F0.wireOp",EDGE,"070828ce-9394-452a-aa16-b4793628ad7e.58.1"),sQuery(id+"F0.wireOp",EDGE,"070828ce-9394-452a-aa16-b4793628ad7e.58.2"),sQuery(id+"F0.wireOp",EDGE,"070828ce-9394-452a-aa16-b4793628ad7e.58.3"),sQuery(id+"F0.wireOp",EDGE,"070828ce-9394-452a-aa16-b4793628ad7e.58.4"),sQuery(id+"F0.wireOp",EDGE,"070828ce-9394-452a-aa16-b4793628ad7e.58.5"),sQuery(id+"F0.wireOp",EDGE,"070828ce-9394-452a-aa16-b4793628ad7e.59.0"),sQuery(id+"F0.wireOp",EDGE,"070828ce-9394-452a-aa16-b4793628ad7e.59.1"),sQuery(id+"F0.wireOp",EDGE,"070828ce-9394-452a-aa16-b4793628ad7e.59.2"),sQuery(id+"F0.wireOp",EDGE,"070828ce-9394-452a-aa16-b4793628ad7e.59.3"),sQuery(id+"F0.wireOp",EDGE,"070828ce-9394-452a-aa16-b4793628ad7e.59.4"),sQuery(id+"F0.wireOp",EDGE,"070828ce-9394-452a-aa16-b4793628ad7e.59.5"),sQuery(id+"F0.wireOp",EDGE,"070828ce-9394-452a-aa16-b4793628ad7e.60.0"),sQuery(id+"F0.wireOp",EDGE,"070828ce-9394-452a-aa16-b4793628ad7e.60.1"),sQuery(id+"F0.wireOp",EDGE,"070828ce-9394-452a-aa16-b4793628ad7e.60.2"),sQuery(id+"F0.wireOp",EDGE,"070828ce-9394-452a-aa16-b4793628ad7e.60.3"),sQuery(id+"F0.wireOp",EDGE,"070828ce-9394-452a-aa16-b4793628ad7e.60.4"),sQuery(id+"F0.wireOp",EDGE,"070828ce-9394-452a-aa16-b4793628ad7e.60.5"),sQuery(id+"F0.wireOp",EDGE,"070828ce-9394-452a-aa16-b4793628ad7e.61.0"),sQuery(id+"F0.wireOp",EDGE,"070828ce-9394-452a-aa16-b4793628ad7e.61.1"),sQuery(id+"F0.wireOp",EDGE,"070828ce-9394-452a-aa16-b4793628ad7e.61.2"),sQuery(id+"F0.wireOp",EDGE,"070828ce-9394-452a-aa16-b4793628ad7e.61.3"),sQuery(id+"F0.wireOp",EDGE,"070828ce-9394-452a-aa16-b4793628ad7e.61.4"),sQuery(id+"F0.wireOp",EDGE,"070828ce-9394-452a-aa16-b4793628ad7e.61.5"),sQuery(id+"F0.wireOp",EDGE,"070828ce-9394-452a-aa16-b4793628ad7e.62.0"),sQuery(id+"F0.wireOp",EDGE,"070828ce-9394-452a-aa16-b4793628ad7e.62.1"),sQuery(id+"F0.wireOp",EDGE,"070828ce-9394-452a-aa16-b4793628ad7e.62.2"),sQuery(id+"F0.wireOp",EDGE,"070828ce-9394-452a-aa16-b4793628ad7e.62.3"),sQuery(id+"F0.wireOp",EDGE,"070828ce-9394-452a-aa16-b4793628ad7e.62.4"),sQuery(id+"F0.wireOp",EDGE,"070828ce-9394-452a-aa16-b4793628ad7e.62.5"),sQuery(id+"F0.wireOp",EDGE,"070828ce-9394-452a-aa16-b4793628ad7e.63.0"),sQuery(id+"F0.wireOp",EDGE,"070828ce-9394-452a-aa16-b4793628ad7e.63.1"),sQuery(id+"F0.wireOp",EDGE,"070828ce-9394-452a-aa16-b4793628ad7e.63.2"),sQuery(id+"F0.wireOp",EDGE,"070828ce-9394-452a-aa16-b4793628ad7e.63.3"),sQuery(id+"F0.wireOp",EDGE,"070828ce-9394-452a-aa16-b4793628ad7e.63.4"),sQuery(id+"F0.wireOp",EDGE,"070828ce-9394-452a-aa16-b4793628ad7e.63.5"),sQuery(id+"F0.wireOp",EDGE,"070828ce-9394-452a-aa16-b4793628ad7e.64.0"),sQuery(id+"F0.wireOp",EDGE,"070828ce-9394-452a-aa16-b4793628ad7e.64.1"),sQuery(id+"F0.wireOp",EDGE,"070828ce-9394-452a-aa16-b4793628ad7e.64.2"),sQuery(id+"F0.wireOp",EDGE,"070828ce-9394-452a-aa16-b4793628ad7e.64.3"),sQuery(id+"F0.wireOp",EDGE,"070828ce-9394-452a-aa16-b4793628ad7e.64.4"),sQuery(id+"F0.wireOp",EDGE,"070828ce-9394-452a-aa16-b4793628ad7e.64.5"),sQuery(id+"F0.wireOp",EDGE,"070828ce-9394-452a-aa16-b4793628ad7e.65.0"),sQuery(id+"F0.wireOp",EDGE,"070828ce-9394-452a-aa16-b4793628ad7e.65.1"),sQuery(id+"F0.wireOp",EDGE,"070828ce-9394-452a-aa16-b4793628ad7e.65.2"),sQuery(id+"F0.wireOp",EDGE,"070828ce-9394-452a-aa16-b4793628ad7e.65.3"),sQuery(id+"F0.wireOp",EDGE,"070828ce-9394-452a-aa16-b4793628ad7e.65.4"),sQuery(id+"F0.wireOp",EDGE,"070828ce-9394-452a-aa16-b4793628ad7e.65.5")])],"isStart":false});
            var sketch = newSketch(context, id + "F2", { "sketchPlane" : qUnion([Q0])});
            skCircle(sketch, "E12", {"center": v(0, 0) * mm, "radius": 3.43 * mm});
            skSolve(sketch);
        }
        {
            var Q0;
            Q0 = qSketchRegion(id + "F2", true);
            extrude(context, id + "F3", {"entities" : qUnion([Q0]), "operationType" : NewBodyOperationType.REMOVE, "oppositeDirection" : true, "depth" : 25.4 * mm, "offsetDistance" : 25.4 * mm});
        }
        {
            var Q0;
            Q0=makeQuery(id+"F1.opExtrude","CAP_FACE",FACE,{"disambiguationData":[OSD([sQuery(id+"F0.wireOp",EDGE,"E0"),sQuery(id+"F0.wireOp",EDGE,"E3"),sQuery(id+"F0.wireOp",EDGE,"E4"),sQuery(id+"F0.wireOp",EDGE,"E5"),sQuery(id+"F0.wireOp",EDGE,"E6.MirrorCS"),sQuery(id+"F0.wireOp",EDGE,"E7.MirrorCS"),sQuery(id+"F0.wireOp",EDGE,"E8.MirrorCS"),sQuery(id+"F0.wireOp",EDGE,"E11.1.0"),sQuery(id+"F0.wireOp",EDGE,"E11.1.1"),sQuery(id+"F0.wireOp",EDGE,"E11.1.2"),sQuery(id+"F0.wireOp",EDGE,"E11.1.3"),sQuery(id+"F0.wireOp",EDGE,"E11.1.4"),sQuery(id+"F0.wireOp",EDGE,"E11.1.5"),sQuery(id+"F0.wireOp",EDGE,"E11.2.0"),sQuery(id+"F0.wireOp",EDGE,"E11.2.1"),sQuery(id+"F0.wireOp",EDGE,"E11.2.2"),sQuery(id+"F0.wireOp",EDGE,"E11.2.3"),sQuery(id+"F0.wireOp",EDGE,"E11.2.4"),sQuery(id+"F0.wireOp",EDGE,"E11.2.5"),sQuery(id+"F0.wireOp",EDGE,"E11.3.0"),sQuery(id+"F0.wireOp",EDGE,"E11.3.1"),sQuery(id+"F0.wireOp",EDGE,"E11.3.2"),sQuery(id+"F0.wireOp",EDGE,"E11.3.3"),sQuery(id+"F0.wireOp",EDGE,"E11.3.4"),sQuery(id+"F0.wireOp",EDGE,"E11.3.5"),sQuery(id+"F0.wireOp",EDGE,"E11.4.0"),sQuery(id+"F0.wireOp",EDGE,"E11.4.1"),sQuery(id+"F0.wireOp",EDGE,"E11.4.2"),sQuery(id+"F0.wireOp",EDGE,"E11.4.3"),sQuery(id+"F0.wireOp",EDGE,"E11.4.4"),sQuery(id+"F0.wireOp",EDGE,"E11.4.5"),sQuery(id+"F0.wireOp",EDGE,"E11.5.0"),sQuery(id+"F0.wireOp",EDGE,"E11.5.1"),sQuery(id+"F0.wireOp",EDGE,"E11.5.2"),sQuery(id+"F0.wireOp",EDGE,"E11.5.3"),sQuery(id+"F0.wireOp",EDGE,"E11.5.4"),sQuery(id+"F0.wireOp",EDGE,"E11.5.5"),sQuery(id+"F0.wireOp",EDGE,"E11.6.0"),sQuery(id+"F0.wireOp",EDGE,"E11.6.1"),sQuery(id+"F0.wireOp",EDGE,"E11.6.2"),sQuery(id+"F0.wireOp",EDGE,"E11.6.3"),sQuery(id+"F0.wireOp",EDGE,"E11.6.4"),sQuery(id+"F0.wireOp",EDGE,"E11.6.5"),sQuery(id+"F0.wireOp",EDGE,"E11.7.0"),sQuery(id+"F0.wireOp",EDGE,"E11.7.1"),sQuery(id+"F0.wireOp",EDGE,"E11.7.2"),sQuery(id+"F0.wireOp",EDGE,"E11.7.3"),sQuery(id+"F0.wireOp",EDGE,"E11.7.4"),sQuery(id+"F0.wireOp",EDGE,"E11.7.5"),sQuery(id+"F0.wireOp",EDGE,"E11.8.0"),sQuery(id+"F0.wireOp",EDGE,"E11.8.1"),sQuery(id+"F0.wireOp",EDGE,"E11.8.2"),sQuery(id+"F0.wireOp",EDGE,"E11.8.3"),sQuery(id+"F0.wireOp",EDGE,"E11.8.4"),sQuery(id+"F0.wireOp",EDGE,"E11.8.5"),sQuery(id+"F0.wireOp",EDGE,"E11.9.0"),sQuery(id+"F0.wireOp",EDGE,"E11.9.1"),sQuery(id+"F0.wireOp",EDGE,"E11.9.2"),sQuery(id+"F0.wireOp",EDGE,"E11.9.3"),sQuery(id+"F0.wireOp",EDGE,"E11.9.4"),sQuery(id+"F0.wireOp",EDGE,"E11.9.5"),sQuery(id+"F0.wireOp",EDGE,"E11.10.0"),sQuery(id+"F0.wireOp",EDGE,"E11.10.1"),sQuery(id+"F0.wireOp",EDGE,"E11.10.2"),sQuery(id+"F0.wireOp",EDGE,"E11.10.3"),sQuery(id+"F0.wireOp",EDGE,"E11.10.4"),sQuery(id+"F0.wireOp",EDGE,"E11.10.5"),sQuery(id+"F0.wireOp",EDGE,"E11.11.0"),sQuery(id+"F0.wireOp",EDGE,"E11.11.1"),sQuery(id+"F0.wireOp",EDGE,"E11.11.2"),sQuery(id+"F0.wireOp",EDGE,"E11.11.3"),sQuery(id+"F0.wireOp",EDGE,"E11.11.4"),sQuery(id+"F0.wireOp",EDGE,"E11.11.5"),sQuery(id+"F0.wireOp",EDGE,"E11.12.0"),sQuery(id+"F0.wireOp",EDGE,"E11.12.1"),sQuery(id+"F0.wireOp",EDGE,"E11.12.2"),sQuery(id+"F0.wireOp",EDGE,"E11.12.3"),sQuery(id+"F0.wireOp",EDGE,"E11.12.4"),sQuery(id+"F0.wireOp",EDGE,"E11.12.5"),sQuery(id+"F0.wireOp",EDGE,"E11.13.0"),sQuery(id+"F0.wireOp",EDGE,"E11.13.1"),sQuery(id+"F0.wireOp",EDGE,"E11.13.2"),sQuery(id+"F0.wireOp",EDGE,"E11.13.3"),sQuery(id+"F0.wireOp",EDGE,"E11.13.4"),sQuery(id+"F0.wireOp",EDGE,"E11.13.5"),sQuery(id+"F0.wireOp",EDGE,"E11.14.0"),sQuery(id+"F0.wireOp",EDGE,"E11.14.1"),sQuery(id+"F0.wireOp",EDGE,"E11.14.2"),sQuery(id+"F0.wireOp",EDGE,"E11.14.3"),sQuery(id+"F0.wireOp",EDGE,"E11.14.4"),sQuery(id+"F0.wireOp",EDGE,"E11.14.5"),sQuery(id+"F0.wireOp",EDGE,"E11.15.0"),sQuery(id+"F0.wireOp",EDGE,"E11.15.1"),sQuery(id+"F0.wireOp",EDGE,"E11.15.2"),sQuery(id+"F0.wireOp",EDGE,"E11.15.3"),sQuery(id+"F0.wireOp",EDGE,"E11.15.4"),sQuery(id+"F0.wireOp",EDGE,"E11.15.5"),sQuery(id+"F0.wireOp",EDGE,"E11.16.0"),sQuery(id+"F0.wireOp",EDGE,"E11.16.1"),sQuery(id+"F0.wireOp",EDGE,"E11.16.2"),sQuery(id+"F0.wireOp",EDGE,"E11.16.3"),sQuery(id+"F0.wireOp",EDGE,"E11.16.4"),sQuery(id+"F0.wireOp",EDGE,"E11.16.5"),sQuery(id+"F0.wireOp",EDGE,"E11.17.0"),sQuery(id+"F0.wireOp",EDGE,"E11.17.1"),sQuery(id+"F0.wireOp",EDGE,"E11.17.2"),sQuery(id+"F0.wireOp",EDGE,"E11.17.3"),sQuery(id+"F0.wireOp",EDGE,"E11.17.4"),sQuery(id+"F0.wireOp",EDGE,"E11.17.5"),sQuery(id+"F0.wireOp",EDGE,"E11.18.0"),sQuery(id+"F0.wireOp",EDGE,"E11.18.1"),sQuery(id+"F0.wireOp",EDGE,"E11.18.2"),sQuery(id+"F0.wireOp",EDGE,"E11.18.3"),sQuery(id+"F0.wireOp",EDGE,"E11.18.4"),sQuery(id+"F0.wireOp",EDGE,"E11.18.5"),sQuery(id+"F0.wireOp",EDGE,"E11.19.0"),sQuery(id+"F0.wireOp",EDGE,"E11.19.1"),sQuery(id+"F0.wireOp",EDGE,"E11.19.2"),sQuery(id+"F0.wireOp",EDGE,"E11.19.3"),sQuery(id+"F0.wireOp",EDGE,"E11.19.4"),sQuery(id+"F0.wireOp",EDGE,"E11.19.5"),sQuery(id+"F0.wireOp",EDGE,"E11.20.0"),sQuery(id+"F0.wireOp",EDGE,"E11.20.1"),sQuery(id+"F0.wireOp",EDGE,"E11.20.2"),sQuery(id+"F0.wireOp",EDGE,"E11.20.3"),sQuery(id+"F0.wireOp",EDGE,"E11.20.4"),sQuery(id+"F0.wireOp",EDGE,"E11.20.5"),sQuery(id+"F0.wireOp",EDGE,"E11.21.0"),sQuery(id+"F0.wireOp",EDGE,"E11.21.1"),sQuery(id+"F0.wireOp",EDGE,"E11.21.2"),sQuery(id+"F0.wireOp",EDGE,"E11.21.3"),sQuery(id+"F0.wireOp",EDGE,"E11.21.4"),sQuery(id+"F0.wireOp",EDGE,"E11.21.5"),sQuery(id+"F0.wireOp",EDGE,"E11.22.0"),sQuery(id+"F0.wireOp",EDGE,"E11.22.1"),sQuery(id+"F0.wireOp",EDGE,"E11.22.2"),sQuery(id+"F0.wireOp",EDGE,"E11.22.3"),sQuery(id+"F0.wireOp",EDGE,"E11.22.4"),sQuery(id+"F0.wireOp",EDGE,"E11.22.5"),sQuery(id+"F0.wireOp",EDGE,"E11.23.0"),sQuery(id+"F0.wireOp",EDGE,"E11.23.1"),sQuery(id+"F0.wireOp",EDGE,"E11.23.2"),sQuery(id+"F0.wireOp",EDGE,"E11.23.3"),sQuery(id+"F0.wireOp",EDGE,"E11.23.4"),sQuery(id+"F0.wireOp",EDGE,"E11.23.5"),sQuery(id+"F0.wireOp",EDGE,"E11.24.0"),sQuery(id+"F0.wireOp",EDGE,"E11.24.1"),sQuery(id+"F0.wireOp",EDGE,"E11.24.2"),sQuery(id+"F0.wireOp",EDGE,"E11.24.3"),sQuery(id+"F0.wireOp",EDGE,"E11.24.4"),sQuery(id+"F0.wireOp",EDGE,"E11.24.5"),sQuery(id+"F0.wireOp",EDGE,"E11.25.0"),sQuery(id+"F0.wireOp",EDGE,"E11.25.1"),sQuery(id+"F0.wireOp",EDGE,"E11.25.2"),sQuery(id+"F0.wireOp",EDGE,"E11.25.3"),sQuery(id+"F0.wireOp",EDGE,"E11.25.4"),sQuery(id+"F0.wireOp",EDGE,"E11.25.5"),sQuery(id+"F0.wireOp",EDGE,"E11.26.0"),sQuery(id+"F0.wireOp",EDGE,"E11.26.1"),sQuery(id+"F0.wireOp",EDGE,"E11.26.2"),sQuery(id+"F0.wireOp",EDGE,"E11.26.3"),sQuery(id+"F0.wireOp",EDGE,"E11.26.4"),sQuery(id+"F0.wireOp",EDGE,"E11.26.5"),sQuery(id+"F0.wireOp",EDGE,"E11.27.0"),sQuery(id+"F0.wireOp",EDGE,"E11.27.1"),sQuery(id+"F0.wireOp",EDGE,"E11.27.2"),sQuery(id+"F0.wireOp",EDGE,"E11.27.3"),sQuery(id+"F0.wireOp",EDGE,"E11.27.4"),sQuery(id+"F0.wireOp",EDGE,"E11.27.5"),sQuery(id+"F0.wireOp",EDGE,"E11.28.0"),sQuery(id+"F0.wireOp",EDGE,"E11.28.1"),sQuery(id+"F0.wireOp",EDGE,"E11.28.2"),sQuery(id+"F0.wireOp",EDGE,"E11.28.3"),sQuery(id+"F0.wireOp",EDGE,"E11.28.4"),sQuery(id+"F0.wireOp",EDGE,"E11.28.5"),sQuery(id+"F0.wireOp",EDGE,"E11.29.0"),sQuery(id+"F0.wireOp",EDGE,"E11.29.1"),sQuery(id+"F0.wireOp",EDGE,"E11.29.2"),sQuery(id+"F0.wireOp",EDGE,"E11.29.3"),sQuery(id+"F0.wireOp",EDGE,"E11.29.4"),sQuery(id+"F0.wireOp",EDGE,"E11.29.5")])],"isStart":false});
            var sketch = newSketch(context, id + "F4", { "sketchPlane" : qUnion([Q0])});
            skCircle(sketch, "E13", {"center": v(0, 0) * mm, "radius": 10.16 * mm});
            skCircle(sketch, "E14", {"center": v(0, 0) * mm, "radius": 5.08 * mm});
            skSolve(sketch);
        }
        {
            var Q0;
            Q0 = qSketchRegion(id + "F4", true);
            extrude(context, id + "F5", {"entities" : qUnion([Q0]), "operationType" : NewBodyOperationType.REMOVE, "oppositeDirection" : true, "depth" : 7.62 * mm, "offsetDistance" : 25.4 * mm});
        }
    });
